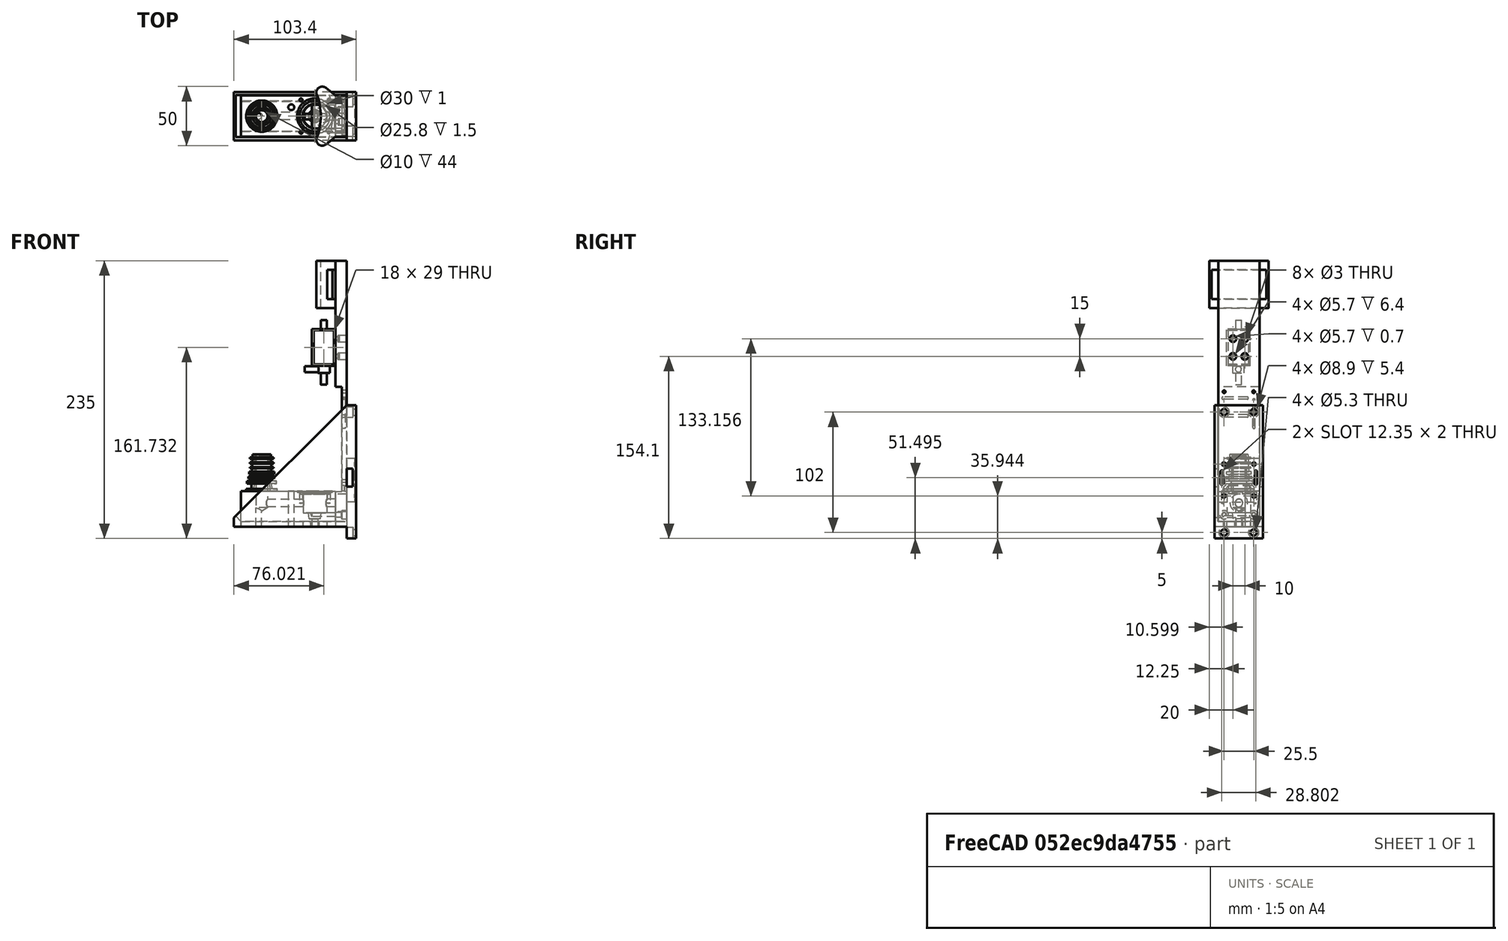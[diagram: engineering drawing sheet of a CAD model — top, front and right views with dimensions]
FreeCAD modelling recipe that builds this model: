
FCSTD DOCUMENT  (FreeCAD 1.0R39109 (Git))
Label: Bottle Nozzle V6
License: All rights reserved
LicenseURL: http://en.wikipedia.org/wiki/All_rights_reserved
objects: Sketcher::SketchObject×31, PartDesign::Pocket×11, PartDesign::Hole×9, PartDesign::Pad×6, Mesh::Feature×5, PartDesign::Body×4, TechDraw::DrawProjGroupItem×3, TechDraw::DrawViewDimension×3, PartDesign::Revolution×2, Spreadsheet::Sheet×1, PartDesign::Groove×1, TechDraw::DrawSVGTemplate×1, TechDraw::DrawPage×1, Part::FeaturePython×1
note: 154 computed .brp shape members not serialized (recipe doc carries the construction recipe); baked Part::Feature solids carry a one-line shape summary decoded from their .brp

FEATURE [Sketcher::SketchObject] Sketch
  ArcFitTolerance = 0
  FullyConstrained = true
  MakeInternals = false
  MapMode = 5
  Placement = pos=(0,0,0) rot=(1,0,0;1.5708rad)
  expr: Constraints[10] = Spreadsheet.HeightPart
  expr: Constraints[12] = Spreadsheet.PartWidth / 2
  expr: Constraints[13] = Spreadsheet.PipeCircle / 2
  expr: Constraints[17] = Spreadsheet.HeigthDop
  expr: Constraints[8] = Spreadsheet.PartWidth2 / 2
  sketch-geometry (8):
    g0: LineSegment StartX=6 StartY=60 StartZ=0 EndX=6.75 EndY=30 EndZ=0
    g1: LineSegment [constr] StartX=6.75 StartY=30 StartZ=0 EndX=17.5 EndY=30 EndZ=0
    g2: LineSegment [constr] StartX=17.5 StartY=30 StartZ=0 EndX=17.5 EndY=0 EndZ=0
    g3: LineSegment [constr] StartX=17.5 StartY=0 StartZ=0 EndX=0 EndY=0 EndZ=0
    g4: LineSegment StartX=0 StartY=60 StartZ=0 EndX=6 EndY=60 EndZ=0
    g5: LineSegment [constr] StartX=0 StartY=60 StartZ=0 EndX=0 EndY=0 EndZ=0
    g6: LineSegment StartX=6.75 StartY=30 StartZ=0 EndX=0 EndY=30 EndZ=0
    g7: LineSegment StartX=0 StartY=30 StartZ=0 EndX=0 EndY=60 EndZ=0
  constraints (23):
    c: Coincident(g0,g1)
    c: Coincident(g1,g2)
    c: Vertical(g2)
    c: Coincident(g2,g3)
    c: Horizontal(g3)
    c: Coincident(g4,g0)
    c: Horizontal(g4)
    c: Horizontal(g1)
    c: DistanceX(g-1,g0) = 6.75
    c: Coincident(g5,g4)
    c: DistanceY(g2,g2) = 30
    c: Vertical(g5)
    c: DistanceX(g-1,g0) = 6
    c: DistanceX(g-1,g2) = 17.5
    c: Coincident(g3,g5)
    c: PointOnObject(g-1,g3)
    c: PointOnObject(g-1,g5)
    c: DistanceY(g1,g0) = 30
    c: Coincident(g6,g0)
    c: PointOnObject(g6,g5)
    c: Horizontal(g6)
    c: Coincident(g7,g6)
    c: Coincident(g7,g4)
FEATURE [PartDesign::Revolution] Revolution
  Angle = 360
  Angle2 = 60
  Axis = (0,2e-16,1)
  Base = (0,0,0)
  Placement = pos=(0,0,0) rot=(1,0,0;1.5708rad)
  Profile = -> Sketch
  ReferenceAxis = -> Sketch [V_Axis]
  Reversed = true
  Suppressed = false
  Type = 0
FEATURE [Spreadsheet::Sheet] Spreadsheet
  cells = A1='DiameterTube; B1(DiameterTube)==5 mm; C1==(B1 / 2) ^ 2 * pi; E1='Outer available; F1==C4 - C1; G1='Similair to inner tube; H1==sqrt(F1 / pi); A2='TubeOffset; B2(TubeOffset)==2.5 mm; C2==(HeightPart - DiameterTube) / 2; A3='DiameterTubeInner; B3(DiameterTubeInner)==B1 - 2 mm; C3==(B3 / 2) ^ 2 * pi; E3='Inner available; F3==C3; H3==sqrt(F3 / pi); A4='DiameterHole; B4(DiameterHole)==10 mm; C4==(B4 / 2) ^ 2 * pi; D4='Max = PartWidth-Walls*2; E4='Ratio liquid VS air surface; F4==F1 / F3; A5='PipeCircle; B5(PipeCircle)==35 mm; A6='HeightPart; B6(HeightPart)==30 mm; A7='HeigthDop; B7(HeigthDop)==30 mm; A8='PartWidth; B8(PartWidth)==12 mm; A9='PartWidth2; B9(PartWidth2)==13.5 mm; A10='MountingHoleDistance; B10(MountingHoleDistance)==round(sqrt((((PipeCircle - PartWidth2) / 2 + PartWidth2) / 2) ^ 2 * 2) / 2.5) * 2.5; A11='OffsetFluidHole2; B11(OffsetFluidHole2)==OffsetFlakte - (4 mm + 0.8 mm * 8 / 2); C11='Blindstop Depth is 3mm+1mm spacer, M5 = 4.2mm; A12='WidthFlank; B12(WidthFlank)==10 mm; A13='OffsetFlakte; B13(OffsetFlakte)==sqrt(PipeCircle ^ 2 - (WidthFlank / 2) ^ 2) / 2 - 0.82 mm; A14='FluidHole; B14(FluidHole)==5 mm; C14='M7; A15='FluidHoleOutsideTube; B15(FluidHoleOutsideTube)==FluidHole + 2 mm; A16='PartOffset; B16(PartOffset)=10; A17='offsetvalve; B17(offsetvalve)=45
FEATURE [Sketcher::SketchObject] Sketch003
  ArcFitTolerance = 0
  AttachmentOffset = pos=(0,0,60) rot=(0,0,1;0rad)
  FullyConstrained = true
  MakeInternals = false
  MapMode = 5
  Placement = pos=(0,0,60) rot=(0,0,1;0rad)
  expr: .AttachmentOffset.Base.z = Spreadsheet.HeightPart + Spreadsheet.HeigthDop
  expr: Constraints[1] = Spreadsheet.DiameterHole
  sketch-geometry (1):
    g0: Circle CenterX=0 CenterY=0 CenterZ=0 NormalX=0 NormalY=0 NormalZ=1 AngleXU=0 Radius=5
  constraints (2):
    c: Coincident(g0,g-1)
    c: Diameter(g0) = 10
FEATURE [Sketcher::SketchObject] Sketch005
  ArcFitTolerance = 0
  FullyConstrained = true
  MakeInternals = false
  MapMode = 5
  expr: Constraints[0] = Spreadsheet.DiameterTube
  expr: Constraints[2] = Spreadsheet.TubeOffset
  sketch-geometry (1):
    g0: Circle CenterX=-2.5 CenterY=0 CenterZ=0 NormalX=0 NormalY=0 NormalZ=1 AngleXU=0 Radius=2.5
  constraints (3):
    c: Diameter(g0) = 5
    c: PointOnObject(g0,g-1)
    c: DistanceX(g0,g-1) = 2.5
FEATURE [Sketcher::SketchObject] Sketch006
  ArcFitTolerance = 0
  FullyConstrained = true
  MakeInternals = false
  MapMode = 5
  expr: Constraints[18] = Spreadsheet.PipeCircle / 2
  expr: Constraints[9] = Spreadsheet.PipeCircle
  sketch-geometry (7):
    g0: LineSegment StartX=0 StartY=17.5 StartZ=0 EndX=62.5 EndY=17.5 EndZ=0
    g1: LineSegment StartX=62.5 StartY=17.5 StartZ=0 EndX=62.5 EndY=-17.5 EndZ=0
    g2: LineSegment StartX=62.5 StartY=-17.5 StartZ=0 EndX=0 EndY=-17.5 EndZ=0
    g3: LineSegment [constr] StartX=0 StartY=-17.5 StartZ=0 EndX=0 EndY=17.5 EndZ=0
    g4: LineSegment StartX=0 StartY=17.5 StartZ=0 EndX=-17.5 EndY=17.5 EndZ=0
    g5: LineSegment StartX=-17.5 StartY=17.5 StartZ=0 EndX=-17.5 EndY=-17.5 EndZ=0
    g6: LineSegment StartX=-17.5 StartY=-17.5 StartZ=0 EndX=0 EndY=-17.5 EndZ=0
  constraints (19):
    c: Coincident(g0,g1)
    c: Coincident(g1,g2)
    c: Coincident(g2,g3)
    c: Coincident(g3,g0)
    c: Horizontal(g0)
    c: Horizontal(g2)
    c: Vertical(g1)
    c: PointOnObject(g0,g-2)
    c: Symmetric(g0,g2,g-1)
    c: DistanceY(g3,g3) = 35
    c: DistanceX(g0,g0) = 62.5  'ww'
    c: Coincident(g0,g4)
    c: Horizontal(g4)
    c: Coincident(g4,g5)
    c: Vertical(g5)
    c: Coincident(g5,g6)
    c: Coincident(g6,g2)
    c: Horizontal(g6)
    c: DistanceX(g4,g4) = 17.5
FEATURE [PartDesign::Pad] Pad
  BaseFeature = -> Revolution
  Direction = (0,0,1)
  Length = 30
  Length2 = 10
  Placement = pos=(0,0,0) rot=(1,0,0;1.5708rad)
  Profile = -> Sketch006
  ReferenceAxis = -> Sketch006 [N_Axis]
  Suppressed = false
  Type = 0
  expr: Length = Spreadsheet.HeightPart
FEATURE [PartDesign::Hole] Hole  label="Hole Combination"
  BaseFeature = -> Pad
  CustomThreadClearance = 0
  Depth = 44
  DepthType = 0
  Diameter = 10
  DrillForDepth = false
  DrillPoint = 1
  DrillPointAngle = 118
  HoleCutCountersinkAngle = 90
  HoleCutCustomValues = false
  HoleCutDepth = 0
  HoleCutDiameter = 10.1
  HoleCutType = 0
  ModelThread = false
  Placement = pos=(0,0,0) rot=(1,0,0;1.5708rad)
  Profile = -> Sketch003
  Suppressed = false
  Tapered = false
  TaperedAngle = 90
  ThreadClass = 0
  ThreadDepth = 44
  ThreadDepthType = 0
  ThreadDirection = 0
  ThreadFit = 0
  ThreadSize = 0
  ThreadType = 0
  Threaded = false
  UseCustomThreadClearance = false
  expr: Depth = 44 mm
FEATURE [PartDesign::Hole] Hole001  label="Hole Air"
  BaseFeature = -> Hole
  CustomThreadClearance = 0
  Depth = 210.228
  DepthType = 1
  Diameter = 5
  DrillForDepth = false
  DrillPoint = 1
  DrillPointAngle = 118
  HoleCutCountersinkAngle = 90
  HoleCutCustomValues = false
  HoleCutDepth = 0
  HoleCutDiameter = 6.1
  HoleCutType = 0
  ModelThread = false
  Placement = pos=(0,0,0) rot=(1,0,0;1.5708rad)
  Profile = -> Sketch005
  Reversed = true
  Suppressed = false
  Tapered = false
  TaperedAngle = 90
  ThreadClass = 0
  ThreadDepth = 210.228
  ThreadDepthType = 0
  ThreadDirection = 0
  ThreadFit = 0
  ThreadSize = 0
  ThreadType = 0
  Threaded = false
  UseCustomThreadClearance = false
FEATURE [Sketcher::SketchObject] Sketch011
  ArcFitTolerance = 0
  AttachmentOffset = pos=(0,0,62.5) rot=(0,0,1;0rad)
  FullyConstrained = true
  MakeInternals = false
  MapMode = 5
  Placement = pos=(62.5,0,0) rot=(0.57735,0.57735,0.57735;2.0944rad)
  expr: .AttachmentOffset.Base.z = Sketch006.Constraints.ww
  expr: .Constraints.hh = 20
  sketch-geometry (1):
    g0: Circle CenterX=0 CenterY=20 CenterZ=0 NormalX=0 NormalY=0 NormalZ=1 AngleXU=0 Radius=4
  constraints (3):
    c: PointOnObject(g0,g-2)
    c: Diameter(g0) = 8
    c: DistanceY(g-1,g0) = 20  'hh'
FEATURE [PartDesign::Hole] Hole002  label="Hole Side"
  BaseFeature = -> Hole001
  CustomThreadClearance = 0
  Depth = 60
  DepthType = 0
  Diameter = 6.4
  DrillForDepth = false
  DrillPoint = 1
  DrillPointAngle = 118
  HoleCutCountersinkAngle = 90
  HoleCutCustomValues = false
  HoleCutDepth = 0
  HoleCutDiameter = 0
  HoleCutType = 0
  ModelThread = false
  Placement = pos=(0,0,0) rot=(1,0,0;1.5708rad)
  Profile = -> Sketch011
  Suppressed = false
  Tapered = false
  TaperedAngle = 90
  ThreadClass = 0
  ThreadDepth = 60
  ThreadDepthType = 0
  ThreadDirection = 0
  ThreadFit = 0
  ThreadSize = 0
  ThreadType = 0
  Threaded = false
  UseCustomThreadClearance = false
  expr: Diameter = 8 * 0.8
FEATURE [Sketcher::SketchObject] Sketch012
  ArcFitTolerance = 0
  AttachmentOffset = pos=(0,0,45) rot=(0,0,1;0rad)
  FullyConstrained = true
  MakeInternals = false
  MapMode = 5
  Placement = pos=(45,0,0) rot=(0.57735,0.57735,0.57735;2.0944rad)
  expr: .AttachmentOffset.Base.z = Spreadsheet.offsetvalve
  expr: Constraints[13] = 25.8 / 2
  expr: Constraints[17] = 20 / 2
  expr: Constraints[24] = 10.8 / 2
  expr: Constraints[25] = 8.6 / 2
  sketch-geometry (15):
    g0: LineSegment StartX=15 StartY=30 StartZ=0 EndX=15 EndY=29 EndZ=0
    g1: LineSegment StartX=15 StartY=29 StartZ=0 EndX=12.9 EndY=29 EndZ=0
    g2: LineSegment StartX=12.9 StartY=29 StartZ=0 EndX=12.9 EndY=27.5 EndZ=0
    g3: LineSegment StartX=12.9 StartY=27.5 StartZ=0 EndX=10.4 EndY=27.5 EndZ=0
    g4: LineSegment StartX=10.4 StartY=27.5 StartZ=0 EndX=10.4 EndY=27.9 EndZ=0
    g5: LineSegment StartX=10 StartY=27.9 StartZ=0 EndX=10 EndY=11.5 EndZ=0
    g6: LineSegment StartX=10 StartY=27.9 StartZ=0 EndX=10.4 EndY=27.9 EndZ=0
    g7: LineSegment StartX=10 StartY=11.5 StartZ=0 EndX=5.4 EndY=11.5 EndZ=0
    g8: LineSegment [constr] StartX=5.4 StartY=11.5 StartZ=0 EndX=4.3 EndY=2.5 EndZ=0
    g9: LineSegment StartX=0 StartY=30 StartZ=0 EndX=0 EndY=0 EndZ=0
    g10: LineSegment StartX=15 StartY=30 StartZ=0 EndX=0 EndY=30 EndZ=0
    g11: LineSegment StartX=2.5 StartY=6.5 StartZ=0 EndX=2.5 EndY=0 EndZ=0
    g12: LineSegment StartX=0 StartY=0 StartZ=0 EndX=2.5 EndY=0 EndZ=0
    g13: LineSegment StartX=5.4 StartY=11.5 StartZ=0 EndX=4.78889 EndY=6.5 EndZ=0
    g14: LineSegment StartX=4.78889 StartY=6.5 StartZ=0 EndX=2.5 EndY=6.5 EndZ=0
  constraints (45):
    c: Vertical(g0)
    c: DistanceY(g-1,g0) = 30
    c: Coincident(g0,g1)
    c: Horizontal(g1)
    c: Coincident(g1,g2)
    c: Vertical(g2)
    c: Coincident(g2,g3)
    c: Coincident(g3,g4)
    c: Vertical(g4)
    c: Vertical(g5)
    c: Horizontal(g3)
    c: DistanceY(g0,g0) = 1
    c: DistanceY(g2,g2) = 1.5
    c: DistanceX(g-1,g1) = 12.9
    c: Coincident(g6,g5)
    c: Coincident(g6,g4)
    c: Horizontal(g6)
    c: DistanceX(g-1,g5) = 10
    c: DistanceY(g4,g4) = 0.4
    c: Equal(g4,g6)
    c: Coincident(g5,g7)
    c: Coincident(g7,g8)
    c: PointOnObject(g9,g-2)
    c: Horizontal(g7)
    c: DistanceX(g-1,g7) = 5.4
    c: DistanceX(g-1,g8) = 4.3
    c: DistanceY(g8,g8) = 9
    c: DistanceY(g5,g3) = 16
    c: DistanceX(g-1,g0) = 15
    c: Coincident(g10,g0)
    c: Coincident(g10,g9)
    c: Horizontal(g10)
    c: DistanceX(g9,g11) = 2.5
    c: PointOnObject(g9,g-2)
    c: PointOnObject(g9,g-1)
    c: PointOnObject(g11,g-1)
    c: Vertical(g11)
    c: Coincident(g12,g9)
    c: Coincident(g12,g11)
    c: Coincident(g13,g7)
    c: PointOnObject(g13,g8)
    c: Coincident(g14,g13)
    c: Horizontal(g14)
    c: DistanceY(g13,g13) = 5
    c: Coincident(g11,g14)
FEATURE [PartDesign::Groove] Groove  label="Groove valve"
  Angle = 360
  Angle2 = 60
  Axis = (1e-16,-1e-16,1)
  Base = (45,0,0)
  BaseFeature = -> Hole002
  Placement = pos=(0,0,0) rot=(1,0,0;1.5708rad)
  Profile = -> Sketch012
  ReferenceAxis = -> Sketch012 [V_Axis]
  Suppressed = false
  Type = 0
FEATURE [Sketcher::SketchObject] Sketch013
  ArcFitTolerance = 0
  AttachmentOffset = pos=(0,0,30) rot=(0,0,1;0rad)
  FullyConstrained = true
  MakeInternals = false
  MapMode = 5
  Placement = pos=(0,0,30) rot=(0,0,1;0rad)
  expr: .AttachmentOffset.Base.z = Spreadsheet.HeightPart
  expr: Constraints[10] = Spreadsheet.offsetvalve
  sketch-geometry (9):
    g0: LineSegment [constr] StartX=33.25 StartY=-13.75 StartZ=0 EndX=33.25 EndY=13.75 EndZ=0
    g1: LineSegment [constr] StartX=33.25 StartY=13.75 StartZ=0 EndX=56.75 EndY=13.75 EndZ=0
    g2: LineSegment [constr] StartX=56.75 StartY=13.75 StartZ=0 EndX=56.75 EndY=-13.75 EndZ=0
    g3: LineSegment [constr] StartX=56.75 StartY=-13.75 StartZ=0 EndX=33.25 EndY=-13.75 EndZ=0
    g4: GeomPoint X=45 Y=-6e-16 Z=0
    g5: Circle CenterX=33.25 CenterY=13.75 CenterZ=0 NormalX=0 NormalY=0 NormalZ=1 AngleXU=0 Radius=1.75
    g6: Circle CenterX=56.75 CenterY=13.75 CenterZ=0 NormalX=0 NormalY=0 NormalZ=1 AngleXU=0 Radius=1.75
    g7: Circle CenterX=33.25 CenterY=-13.75 CenterZ=0 NormalX=0 NormalY=0 NormalZ=1 AngleXU=0 Radius=1.75
    g8: Circle CenterX=56.75 CenterY=-13.75 CenterZ=0 NormalX=0 NormalY=0 NormalZ=1 AngleXU=0 Radius=1.75
  constraints (21):
    c: Coincident(g0,g1)
    c: Coincident(g1,g2)
    c: Coincident(g2,g3)
    c: Coincident(g3,g0)
    c: Horizontal(g1)
    c: Horizontal(g3)
    c: Vertical(g0)
    c: Vertical(g2)
    c: Symmetric(g1,g0,g4)
    c: PointOnObject(g4,g-1)
    c: DistanceX(g-1,g4) = 45
    c: Coincident(g5,g0)
    c: DistanceX(g1,g1) = 23.5
    c: DistanceY(g2,g2) = 27.5
    c: Coincident(g6,g1)
    c: Coincident(g7,g0)
    c: Coincident(g8,g2)
    c: Equal(g5,g6)
    c: Equal(g6,g7)
    c: Equal(g7,g8)
    c: Diameter(g6) = 3.5
FEATURE [PartDesign::Hole] Hole003  label="Hole mouting valve thread"
  BaseFeature = -> Groove
  CustomThreadClearance = 0
  Depth = 10
  DepthType = 0
  Diameter = 2.5
  DrillForDepth = false
  DrillPoint = 1
  DrillPointAngle = 118
  HoleCutCountersinkAngle = 90
  HoleCutCustomValues = false
  HoleCutDepth = 0
  HoleCutDiameter = 6.1
  HoleCutType = 0
  ModelThread = false
  Placement = pos=(0,0,0) rot=(1,0,0;1.5708rad)
  Profile = -> Sketch013
  Suppressed = false
  Tapered = false
  TaperedAngle = 90
  ThreadClass = 0
  ThreadDepth = 10
  ThreadDepthType = 0
  ThreadDirection = 0
  ThreadFit = 0
  ThreadSize = 9
  ThreadType = 1
  Threaded = true
  UseCustomThreadClearance = false
FEATURE [Sketcher::SketchObject] Sketch014
  ArcFitTolerance = 0
  AttachmentOffset = pos=(0,0,62.5) rot=(0,0,1;0rad)
  FullyConstrained = false
  MakeInternals = false
  MapMode = 5
  Placement = pos=(62.5,0,0) rot=(0.57735,0.57735,0.57735;2.0944rad)
  expr: .AttachmentOffset.Base.z = Sketch006.Constraints.ww
  expr: Constraints[1] = Sketch011.Constraints.hh
  sketch-geometry (1):
    g0: Circle CenterX=0 CenterY=20 CenterZ=0 NormalX=0 NormalY=0 NormalZ=1 AngleXU=0 Radius=3.71689
  constraints (2):
    c: PointOnObject(g0,g-2)
    c: DistanceY(g-1,g0) = 20
FEATURE [PartDesign::Hole] Hole004  label="Hole Side thread"
  BaseFeature = -> Hole003
  CustomThreadClearance = 0
  Depth = 20
  DepthType = 0
  Diameter = 6.8
  DrillForDepth = false
  DrillPoint = 1
  DrillPointAngle = 118
  HoleCutCountersinkAngle = 90
  HoleCutCustomValues = false
  HoleCutDepth = 0
  HoleCutDiameter = 6.1
  HoleCutType = 0
  ModelThread = false
  Placement = pos=(0,0,0) rot=(1,0,0;1.5708rad)
  Profile = -> Sketch014
  Suppressed = false
  Tapered = false
  TaperedAngle = 90
  ThreadClass = 0
  ThreadDepth = 20
  ThreadDepthType = 0
  ThreadDirection = 0
  ThreadFit = 0
  ThreadSize = 16
  ThreadType = 1
  Threaded = true
  UseCustomThreadClearance = false
FEATURE [Sketcher::SketchObject] Sketch015
  ArcFitTolerance = 0
  AttachmentOffset = pos=(0,0,4.5) rot=(0,0,1;0rad)
  FullyConstrained = true
  MakeInternals = false
  MapMode = 5
  Placement = pos=(0,0,4.5) rot=(0,0,1;0rad)
  expr: Constraints[14] = Spreadsheet.PipeCircle
  expr: Constraints[15] = Sketch006.Constraints.ww
  expr: Constraints[2] = Spreadsheet.offsetvalve
  sketch-geometry (14):
    g0: Circle CenterX=45 CenterY=0 CenterZ=0 NormalX=0 NormalY=0 NormalZ=1 AngleXU=0 Radius=10
    g1: Circle CenterX=45 CenterY=0 CenterZ=0 NormalX=0 NormalY=0 NormalZ=1 AngleXU=0 Radius=3.5
    g2: LineSegment [constr] StartX=0 StartY=17.5 StartZ=0 EndX=62.5 EndY=17.5 EndZ=0
    g3: LineSegment [constr] StartX=62.5 StartY=17.5 StartZ=0 EndX=62.5 EndY=-17.5 EndZ=0
    g4: LineSegment [constr] StartX=62.5 StartY=-17.5 StartZ=0 EndX=0 EndY=-17.5 EndZ=0
    g5: LineSegment [constr] StartX=0 StartY=-17.5 StartZ=0 EndX=0 EndY=17.5 EndZ=0
    g6: LineSegment StartX=62.5 StartY=17.5 StartZ=0 EndX=-50 EndY=17.5 EndZ=0
    g7: LineSegment StartX=-50 StartY=17.5 StartZ=0 EndX=-50 EndY=12.5 EndZ=0
    g8: LineSegment StartX=-50 StartY=12.5 StartZ=0 EndX=62.5 EndY=12.5 EndZ=0
    g9: LineSegment StartX=62.5 StartY=12.5 StartZ=0 EndX=62.5 EndY=17.5 EndZ=0
    g10: LineSegment StartX=62.5 StartY=-17.5 StartZ=0 EndX=-50 EndY=-17.5 EndZ=0
    g11: LineSegment StartX=-50 StartY=-17.5 StartZ=0 EndX=-50 EndY=-12.5 EndZ=0
    g12: LineSegment StartX=-50 StartY=-12.5 StartZ=0 EndX=62.5 EndY=-12.5 EndZ=0
    g13: LineSegment StartX=62.5 StartY=-12.5 StartZ=0 EndX=62.5 EndY=-17.5 EndZ=0
  constraints (38):
    c: PointOnObject(g0,g-1)
    c: Coincident(g1,g0)
    c: DistanceX(g-1,g0) = 45
    c: Diameter(g1) = 7
    c: Diameter(g0) = 20
    c: Coincident(g2,g3)
    c: Coincident(g3,g4)
    c: Coincident(g4,g5)
    c: Coincident(g5,g2)
    c: Horizontal(g2)
    c: Horizontal(g4)
    c: Vertical(g5)
    c: PointOnObject(g2,g-2)
    c: Symmetric(g2,g3,g-1)
    c: DistanceY(g3,g3) = 35
    c: DistanceX(g2,g2) = 62.5
    c: Coincident(g6,g7)
    c: Coincident(g7,g8)
    c: Coincident(g8,g9)
    c: Coincident(g9,g6)
    c: Horizontal(g6)
    c: Horizontal(g8)
    c: Vertical(g7)
    c: Vertical(g9)
    c: Coincident(g6,g2)
    c: Coincident(g10,g11)
    c: Coincident(g11,g12)
    c: Coincident(g12,g13)
    c: Coincident(g13,g10)
    c: Horizontal(g10)
    c: Horizontal(g12)
    c: Vertical(g11)
    c: Vertical(g13)
    c: Coincident(g10,g3)
    c: Vertical(g11,g7)
    c: DistanceY(g12,g8) = 25
    c: Equal(g7,g11)
    c: DistanceX(g6,g2) = 50
FEATURE [PartDesign::Pocket] Pocket001  label="Pocket fluid outlet pipe"
  BaseFeature = -> Hole004
  Direction = (0,0,-1)
  Length = 5
  Length2 = 5
  Placement = pos=(0,0,0) rot=(1,0,0;1.5708rad)
  Profile = -> Sketch015
  ReferenceAxis = -> Sketch015 [N_Axis]
  Suppressed = false
  Type = 0
FEATURE [Sketcher::SketchObject] Sketch016
  ArcFitTolerance = 0
  AttachmentOffset = pos=(0,0,62.5) rot=(0,0,1;0rad)
  FullyConstrained = false
  MakeInternals = false
  MapMode = 5
  Placement = pos=(62.5,0,0) rot=(0.57735,0.57735,0.57735;2.0944rad)
  sketch-geometry (9):
    g0: LineSegment [constr] StartX=-12.5 StartY=10 StartZ=0 EndX=12.5 EndY=10 EndZ=0
    g1: LineSegment [constr] StartX=12.5 StartY=10 StartZ=0 EndX=12.5 EndY=25 EndZ=0
    g2: LineSegment [constr] StartX=12.5 StartY=25 StartZ=0 EndX=-12.5 EndY=25 EndZ=0
    g3: LineSegment [constr] StartX=-12.5 StartY=25 StartZ=0 EndX=-12.5 EndY=10 EndZ=0
    g4: GeomPoint [constr] X=0 Y=17.5 Z=0
    g5: Circle [constr] CenterX=12.5 CenterY=25 CenterZ=0 NormalX=0 NormalY=0 NormalZ=1 AngleXU=0 Radius=2.9952
    g6: Circle [constr] CenterX=-12.5 CenterY=25 CenterZ=0 NormalX=0 NormalY=0 NormalZ=1 AngleXU=0 Radius=2.9952
    g7: Circle CenterX=-12.5 CenterY=10 CenterZ=0 NormalX=0 NormalY=0 NormalZ=1 AngleXU=0 Radius=2.9952
    g8: Circle CenterX=12.5 CenterY=10 CenterZ=0 NormalX=0 NormalY=0 NormalZ=1 AngleXU=0 Radius=2.9952
  constraints (20):
    c: Coincident(g0,g1)
    c: Coincident(g1,g2)
    c: Coincident(g2,g3)
    c: Coincident(g3,g0)
    c: Horizontal(g0)
    c: Horizontal(g2)
    c: Vertical(g1)
    c: Vertical(g3)
    c: Symmetric(g2,g0,g4)
    c: PointOnObject(g4,g-2)
    c: DistanceX(g2,g2) = 25
    c: DistanceY(g1,g1) = 15
    c: Coincident(g5,g1)
    c: Coincident(g6,g2)
    c: Coincident(g7,g0)
    c: Coincident(g8,g0)
    c: Equal(g5,g8)
    c: Equal(g8,g7)
    c: Equal(g7,g6)
    c: DistanceY(g-1,g0) = 10
FEATURE [PartDesign::Hole] Hole005  label="Hole bottle holder mounting"
  BaseFeature = -> Pocket001
  CustomThreadClearance = 0
  Depth = 20
  DepthType = 0
  Diameter = 3.2
  DrillForDepth = false
  DrillPoint = 1
  DrillPointAngle = 118
  HoleCutCountersinkAngle = 90
  HoleCutCustomValues = false
  HoleCutDepth = 0
  HoleCutDiameter = 6.1
  HoleCutType = 0
  ModelThread = false
  Placement = pos=(0,0,0) rot=(1,0,0;1.5708rad)
  Profile = -> Sketch016
  Refine = true
  Suppressed = false
  Tapered = false
  TaperedAngle = 90
  ThreadClass = 0
  ThreadDepth = 20
  ThreadDepthType = 0
  ThreadDirection = 0
  ThreadFit = 0
  ThreadSize = 0
  ThreadType = 0
  Threaded = false
  UseCustomThreadClearance = false
  expr: Diameter = 0.8 * 4
FEATURE [Sketcher::SketchObject] Sketch018
  ArcFitTolerance = 0
  FullyConstrained = true
  MakeInternals = false
  MapMode = 5
  Placement = pos=(0,0,0) rot=(1,0,0;1.5708rad)
  expr: .Constraints.width = 71.9
  sketch-geometry (15):
    g0: LineSegment StartX=71.9 StartY=102.9 StartZ=0 EndX=-23.5 EndY=7.5 EndZ=0
    g1: LineSegment StartX=-23.5 StartY=7.5 StartZ=0 EndX=-23.5 EndY=0 EndZ=0
    g2: LineSegment StartX=-23.5 StartY=0 StartZ=0 EndX=71.9 EndY=0 EndZ=0
    g3: LineSegment [constr] StartX=71.9 StartY=0 StartZ=0 EndX=71.9 EndY=102.9 EndZ=0
    g4: LineSegment StartX=71.9 StartY=0 StartZ=0 EndX=71.9 EndY=-10 EndZ=0
    g5: Circle [constr] CenterX=-20.7041 CenterY=3.75 CenterZ=0 NormalX=0 NormalY=0 NormalZ=1 AngleXU=0 Radius=1.6
    g6: LineSegment [constr] StartX=-23.5 StartY=7.5 StartZ=0 EndX=-20.5 EndY=7.5 EndZ=0
    g7: LineSegment [constr] StartX=-20.5 StartY=7.5 StartZ=0 EndX=-17.5 EndY=4.5 EndZ=0
    g8: LineSegment [constr] StartX=-23.5 StartY=0 StartZ=0 EndX=-20.7041 EndY=3.75 EndZ=0
    g9: LineSegment [constr] StartX=-20.7041 StartY=3.75 StartZ=0 EndX=-23.5 EndY=7.5 EndZ=0
    g10: LineSegment [constr] StartX=-23.5 StartY=3.75 StartZ=0 EndX=-22.3041 EndY=3.75 EndZ=0
    g11: LineSegment [constr] StartX=-18.727 StartY=5.72703 StartZ=0 EndX=-19.5727 EndY=4.88137 EndZ=0
    g12: LineSegment StartX=71.9 StartY=102.9 StartZ=0 EndX=79.9 EndY=102.9 EndZ=0
    g13: LineSegment StartX=79.9 StartY=102.9 StartZ=0 EndX=79.9 EndY=-10 EndZ=0
    g14: LineSegment StartX=71.9 StartY=-10 StartZ=0 EndX=79.9 EndY=-10 EndZ=0
  constraints (45):
    c: Coincident(g0,g1)
    c: Coincident(g1,g2)
    c: PointOnObject(g3,g-1)
    c: Vertical(g3)
    c: Vertical(g4)
    c: DistanceX(g1,g-1) = 23.5
    c: DistanceY(g1,g1) = 7.5
    c: DistanceX(g-1,g3) = 71.9  'width'
    c: PointOnObject(g-1,g2)
    c: Horizontal(g2)
    c: Vertical(g1)
    c: Coincident(g4,g2)
    c: Vertical(g0,g2)
    c: Angle(g2,g0) = 0.785398
    c: DistanceY(g4,g4) = 10  'MountingHeight'
    c: Diameter(g5) = 3.2
    c: Coincident(g6,g0)
    c: Horizontal(g6)
    c: Coincident(g7,g6)
    c: DistanceX(g6,g6) = 3
    c: DistanceX(g7,g7) = 3
    c: DistanceY(g7,g7) = 3
    c: Coincident(g8,g1)
    c: Coincident(g8,g5)
    c: Coincident(g9,g5)
    c: Coincident(g9,g0)
    c: Equal(g9,g8)
    c: PointOnObject(g10,g1)
    c: PointOnObject(g10,g5)
    c: Horizontal(g10)
    c: PointOnObject(g11,g7)
    c: PointOnObject(g11,g5)
    c: Perpendicular(g7,g11)
    c: Equal(g10,g11)
    c: PointOnObject(g5,g10)
    c: PointOnObject(g5,g11)
    c: Horizontal(g12)
    c: Distance(g12,g12) = 8
    c: Coincident(g12,g13)
    c: Vertical(g13)
    c: Coincident(g14,g4)
    c: Coincident(g14,g13)
    c: Horizontal(g14)
    c: Coincident(g0,g12)
    c: Coincident(g3,g0)
FEATURE [PartDesign::Pad] Pad001  label="Pad all"
  Direction = (0,-1,2e-16)
  Length = 41
  Length2 = 10
  Midplane = true
  Placement = pos=(0,0,0) rot=(1,0,0;1.5708rad)
  Profile = -> Sketch018
  ReferenceAxis = -> Sketch018 [N_Axis]
  Suppressed = false
  Type = 0
  expr: Length = 35 + 3 * 2
FEATURE [Sketcher::SketchObject] Sketch019
  ArcFitTolerance = 0
  FullyConstrained = true
  MakeInternals = false
  MapMode = 5
  Placement = pos=(0,0,0) rot=(1,0,0;1.5708rad)
  expr: Constraints[3] = Sketch018.Constraints.width
  sketch-geometry (5):
    g0: LineSegment StartX=-17.5 StartY=4.5 StartZ=0 EndX=71.9 EndY=4.5 EndZ=0
    g1: LineSegment StartX=71.9 StartY=4.5 StartZ=0 EndX=71.9 EndY=104.5 EndZ=0
    g2: LineSegment StartX=-17.5 StartY=4.5 StartZ=0 EndX=-27.5 EndY=14.5 EndZ=0
    g3: LineSegment StartX=-27.5 StartY=14.5 StartZ=0 EndX=-27.5 EndY=104.5 EndZ=0
    g4: LineSegment StartX=-27.5 StartY=104.5 StartZ=0 EndX=71.9 EndY=104.5 EndZ=0
  constraints (15):
    c: Horizontal(g0)
    c: Coincident(g0,g1)
    c: Vertical(g1)
    c: DistanceX(g-1,g1) = 71.9
    c: DistanceY(g-1,g0) = 4.5
    c: Coincident(g3,g2)
    c: Vertical(g3)
    c: DistanceX(g0,g-1) = 17.5
    c: Coincident(g4,g3)
    c: Coincident(g4,g1)
    c: Horizontal(g4)
    c: Angle(g0,g2) = 2.35619
    c: Coincident(g2,g0)
    c: DistanceX(g2,g2) = 10
    c: DistanceY(g1,g1) = 100
FEATURE [PartDesign::Pocket] Pocket  label="Pocket 1"
  BaseFeature = -> Pad001
  Direction = (0,1,-2e-16)
  Length = 35.6
  Length2 = 5
  Midplane = true
  Placement = pos=(0,0,0) rot=(1,0,0;1.5708rad)
  Profile = -> Sketch019
  ReferenceAxis = -> Sketch019 [N_Axis]
  Suppressed = false
  Type = 0
  expr: Length = 35 + 0.6
FEATURE [Sketcher::SketchObject] Sketch020
  ArcFitTolerance = 0
  FullyConstrained = true
  MakeInternals = false
  MapMode = 5
  Placement = pos=(0,0,0) rot=(1,0,0;1.5708rad)
  expr: Constraints[10] = 17.5 mm + 0.25 mm
  expr: Constraints[11] = Sketch018.Constraints.width
  sketch-geometry (4):
    g0: LineSegment StartX=-17.75 StartY=5 StartZ=0 EndX=71.9 EndY=5 EndZ=0
    g1: LineSegment StartX=71.9 StartY=5 StartZ=0 EndX=71.9 EndY=0 EndZ=0
    g2: LineSegment StartX=71.9 StartY=0 StartZ=0 EndX=-17.75 EndY=0 EndZ=0
    g3: LineSegment StartX=-17.75 StartY=0 StartZ=0 EndX=-17.75 EndY=5 EndZ=0
  constraints (12):
    c: Coincident(g0,g1)
    c: Coincident(g1,g2)
    c: Coincident(g2,g3)
    c: Coincident(g3,g0)
    c: Horizontal(g0)
    c: Horizontal(g2)
    c: Vertical(g1)
    c: Vertical(g3)
    c: PointOnObject(g1,g-1)
    c: DistanceY(g3,g3) = 5
    c: DistanceX(g2,g-1) = 17.75
    c: DistanceX(g-1,g1) = 71.9
FEATURE [PartDesign::Pocket] Pocket002  label="Pocket 2"
  BaseFeature = -> Pocket
  Direction = (0,1,-2e-16)
  Length = 25.6
  Length2 = 5
  Midplane = true
  Placement = pos=(0,0,0) rot=(1,0,0;1.5708rad)
  Profile = -> Sketch020
  ReferenceAxis = -> Sketch020 [N_Axis]
  Suppressed = false
  Type = 0
  expr: Length = 25 + 0.6
FEATURE [Sketcher::SketchObject] Sketch021
  ArcFitTolerance = 0
  AttachmentOffset = pos=(0,0,69.5) rot=(0,0,1;0rad)
  FullyConstrained = false
  MakeInternals = false
  MapMode = 5
  Placement = pos=(71.9,0,0) rot=(0.57735,0.57735,0.57735;2.0944rad)
  expr: .Placement.Base.x = Sketch018.Constraints.width
  expr: Constraints[9] = Sketch018.Constraints.MountingHeight / 2
  sketch-geometry (4):
    g0: Circle CenterX=-12.5 CenterY=97 CenterZ=0 NormalX=0 NormalY=0 NormalZ=1 AngleXU=0 Radius=1.77352
    g1: Circle CenterX=12.5 CenterY=97 CenterZ=0 NormalX=0 NormalY=0 NormalZ=1 AngleXU=0 Radius=1.77352
    g2: Circle CenterX=-12.5 CenterY=-5 CenterZ=0 NormalX=0 NormalY=0 NormalZ=1 AngleXU=0 Radius=1.77352
    g3: Circle CenterX=12.5 CenterY=-5 CenterZ=0 NormalX=0 NormalY=0 NormalZ=1 AngleXU=0 Radius=1.77352
  constraints (10):
    c: Symmetric(g0,g1,g-2)
    c: DistanceX(g0,g1) = 25
    c: Equal(g0,g1)
    c: DistanceY(g-1,g1) = 97
    c: Horizontal(g2,g3)
    c: Vertical(g0,g2)
    c: Vertical(g3,g1)
    c: Equal(g0,g2)
    c: Equal(g3,g2)
    c: DistanceY(g2,g-1) = 5
FEATURE [PartDesign::Hole] Hole006  label="Mounting holes"
  BaseFeature = -> Pocket002
  CustomThreadClearance = 0
  Depth = 320.149
  DepthType = 1
  Diameter = 5.3
  DrillForDepth = false
  DrillPoint = 1
  DrillPointAngle = 118
  HoleCutCountersinkAngle = 90
  HoleCutCustomValues = false
  HoleCutDepth = 5.4
  HoleCutDiameter = 8.9
  HoleCutType = 1
  ModelThread = false
  Placement = pos=(0,0,0) rot=(1,0,0;1.5708rad)
  Profile = -> Sketch021
  Reversed = true
  Suppressed = false
  Tapered = false
  TaperedAngle = 90
  ThreadClass = 0
  ThreadDepth = 320.149
  ThreadDepthType = 0
  ThreadDirection = 0
  ThreadFit = 0
  ThreadSize = 0
  ThreadType = 0
  Threaded = false
  UseCustomThreadClearance = false
FEATURE [Sketcher::SketchObject] Sketch022
  ArcFitTolerance = 0
  AttachmentOffset = pos=(0,0,62.5) rot=(0,0,1;0rad)
  FullyConstrained = true
  MakeInternals = false
  MapMode = 5
  Placement = pos=(62.5,0,0) rot=(0.57735,0.57735,0.57735;2.0944rad)
  expr: .Constraints.Width = 35 mm
  expr: .Constraints.magA = 20.2 mm + 0.2 mm * 2
  expr: .Constraints.magA2 = 4.2 mm + 0.2 mm * 2
  expr: Constraints[12] = 4.5 mm + 0.2 mm
  expr: Constraints[23] = 5 + 0.2
  expr: Constraints[57] = 0.75 * 3
  expr: Constraints[59] = 29.5 - 4.5
  expr: Constraints[60] = 84 - 8.25
  sketch-geometry (24):
    g0: LineSegment StartX=-17.5 StartY=225 StartZ=0 EndX=-17.5 EndY=4.7 EndZ=0
    g1: LineSegment StartX=-12.3 StartY=0 StartZ=0 EndX=12.3 EndY=0 EndZ=0
    g2: LineSegment StartX=17.5 StartY=4.7 StartZ=0 EndX=17.5 EndY=225 EndZ=0
    g3: LineSegment StartX=17.5 StartY=225 StartZ=0 EndX=-17.5 EndY=225 EndZ=0
    g4: GeomPoint [constr] X=0 Y=76.325 Z=0
    g5: LineSegment StartX=-12.3 StartY=4.7 StartZ=0 EndX=-12.3 EndY=0 EndZ=0
    g6: LineSegment StartX=12.3 StartY=0 StartZ=0 EndX=12.3 EndY=4.7 EndZ=0
    g7: LineSegment StartX=-17.5 StartY=4.7 StartZ=0 EndX=-12.3 EndY=4.7 EndZ=0
    g8: LineSegment StartX=12.3 StartY=4.7 StartZ=0 EndX=17.5 EndY=4.7 EndZ=0
    g9: ArcOfCircle CenterX=-8 CenterY=32.4 CenterZ=0 NormalX=0 NormalY=0 NormalZ=1 AngleXU=0 Radius=2.3 StartAngle=1.5708 EndAngle=4.71239
    g10: ArcOfCircle CenterX=8 CenterY=32.4 CenterZ=0 NormalX=0 NormalY=0 NormalZ=1 AngleXU=0 Radius=2.3 StartAngle=4.71239 EndAngle=7.85398
    g11: LineSegment StartX=-8 StartY=34.7 StartZ=0 EndX=8 EndY=34.7 EndZ=0
    g12: LineSegment StartX=-8 StartY=30.1 StartZ=0 EndX=8 EndY=30.1 EndZ=0
    g13: LineSegment [constr] StartX=-10.3 StartY=32.4 StartZ=0 EndX=10.3 EndY=32.4 EndZ=0
    g14: Circle CenterX=0 CenterY=20 CenterZ=0 NormalX=0 NormalY=0 NormalZ=1 AngleXU=0 Radius=7.5
    g15: LineSegment [constr] StartX=-12.5 StartY=38.45 StartZ=0 EndX=12.5 EndY=38.45 EndZ=0
    g16: LineSegment [constr] StartX=12.5 StartY=38.45 StartZ=0 EndX=12.5 EndY=114.2 EndZ=0
    g17: LineSegment [constr] StartX=12.5 StartY=114.2 StartZ=0 EndX=-12.5 EndY=114.2 EndZ=0
    g18: LineSegment [constr] StartX=-12.5 StartY=114.2 StartZ=0 EndX=-12.5 EndY=38.45 EndZ=0
    g19: GeomPoint [constr] X=0 Y=76.325 Z=0
    g20: Circle CenterX=-12.5 CenterY=114.2 CenterZ=0 NormalX=0 NormalY=0 NormalZ=1 AngleXU=0 Radius=1.125
    g21: Circle CenterX=12.5 CenterY=114.2 CenterZ=0 NormalX=0 NormalY=0 NormalZ=1 AngleXU=0 Radius=1.125
    g22: Circle CenterX=-12.5 CenterY=38.45 CenterZ=0 NormalX=0 NormalY=0 NormalZ=1 AngleXU=0 Radius=1.125
    g23: Circle CenterX=12.5 CenterY=38.45 CenterZ=0 NormalX=0 NormalY=0 NormalZ=1 AngleXU=0 Radius=1.125
  constraints (61):
    c: Coincident(g2,g3)
    c: Coincident(g3,g0)
    c: Vertical(g0)
    c: Vertical(g2)
    c: Horizontal(g1)
    c: Horizontal(g3)
    c: PointOnObject(g4,g-2)
    c: Vertical(g5)
    c: Vertical(g6)
    c: Coincident(g1,g5)
    c: Coincident(g1,g6)
    c: DistanceX(g0,g2) = 35  'Width'
    c: DistanceY(g6,g6) = 4.7
    c: PointOnObject(g-1,g1)
    c: Symmetric(g2,g0,g-2)
    c: DistanceY(g-1,g2) = 225  'height'
    c: Coincident(g7,g0)
    c: Horizontal(g7)
    c: Coincident(g8,g6)
    c: Coincident(g8,g2)
    c: Horizontal(g8)
    c: Equal(g7,g8)
    c: Coincident(g5,g7)
    c: DistanceX(g8,g8) = 5.2
    c: Tangent(g9,g11) = 1.5708
    c: Tangent(g9,g12) = -1.5708
    c: Tangent(g10,g11) = 1.5708
    c: Tangent(g10,g12) = -1.5708
    c: Equal(g9,g10)
    c: Symmetric(g10,g9,g-2)
    c: DistanceY(g9,g9) = 4.6  'magA2'
    c: Horizontal(g13)
    c: PointOnObject(g13,g9)
    c: PointOnObject(g13,g10)
    c: PointOnObject(g9,g13)
    c: DistanceX(g13,g13) = 20.6  'magA'
    c: DistanceY(g-1,g9) = 32.4  'magnetoffset'
    c: PointOnObject(g14,g-2)
    c: DistanceY(g-1,g14) = 20
    c: Diameter(g14) = 15
    c: Coincident(g15,g16)
    c: Coincident(g16,g17)
    c: Coincident(g17,g18)
    c: Coincident(g18,g15)
    c: Horizontal(g15)
    c: Horizontal(g17)
    c: Vertical(g16)
    c: Vertical(g18)
    c: Symmetric(g17,g15,g19)
    c: Coincident(g19,g4)
    c: Coincident(g20,g17)
    c: Coincident(g21,g16)
    c: Coincident(g22,g15)
    c: Coincident(g23,g15)
    c: Equal(g22,g23)
    c: Equal(g23,g21)
    c: Equal(g21,g20)
    c: Diameter(g20) = 2.25
    c: DistanceY(g-1,g17) = 114.2
    c: DistanceX(g17,g17) = 25
    c: DistanceY(g18,g18) = 75.75
FEATURE [PartDesign::Pad] Pad002  label="Pad All"
  Direction = (1,1e-16,-1e-16)
  Length = 9.4
  Length2 = 10
  Placement = pos=(62.5,0,0) rot=(0.57735,0.57735,0.57735;2.0944rad)
  Profile = -> Sketch022
  ReferenceAxis = -> Sketch022 [N_Axis]
  Refine = true
  Suppressed = false
  Type = 0
FEATURE [Sketcher::SketchObject] Sketch023
  ArcFitTolerance = 0
  AttachmentOffset = pos=(0,0,69.5) rot=(0,0,1;0rad)
  FullyConstrained = true
  MakeInternals = false
  MapMode = 5
  Placement = pos=(71.9,0,0) rot=(0.57735,0.57735,0.57735;2.0944rad)
  expr: .AttachmentOffset.Base.z = 62.5 mm + 7 mm
  expr: .Placement.Base.x = Sketch018.Constraints.width
  sketch-geometry (9):
    g0: LineSegment [constr] StartX=-12.5 StartY=10 StartZ=0 EndX=12.5 EndY=10 EndZ=0
    g1: LineSegment [constr] StartX=12.5 StartY=10 StartZ=0 EndX=12.5 EndY=25 EndZ=0
    g2: LineSegment [constr] StartX=12.5 StartY=25 StartZ=0 EndX=-12.5 EndY=25 EndZ=0
    g3: LineSegment [constr] StartX=-12.5 StartY=25 StartZ=0 EndX=-12.5 EndY=10 EndZ=0
    g4: GeomPoint [constr] X=0 Y=17.5 Z=0
    g5: Circle [constr] CenterX=-12.5 CenterY=25 CenterZ=0 NormalX=0 NormalY=0 NormalZ=1 AngleXU=0 Radius=2.5
    g6: Circle CenterX=-12.5 CenterY=10 CenterZ=0 NormalX=0 NormalY=0 NormalZ=1 AngleXU=0 Radius=2.5
    g7: Circle CenterX=12.5 CenterY=10 CenterZ=0 NormalX=0 NormalY=0 NormalZ=1 AngleXU=0 Radius=2.5
    g8: Circle [constr] CenterX=12.5 CenterY=25 CenterZ=0 NormalX=0 NormalY=0 NormalZ=1 AngleXU=0 Radius=2.5
  constraints (21):
    c: Coincident(g0,g1)
    c: Coincident(g1,g2)
    c: Coincident(g2,g3)
    c: Coincident(g3,g0)
    c: Horizontal(g0)
    c: Horizontal(g2)
    c: Vertical(g1)
    c: Vertical(g3)
    c: Symmetric(g2,g0,g4)
    c: PointOnObject(g4,g-2)
    c: DistanceX(g2,g2) = 25
    c: DistanceY(g1,g1) = 15
    c: DistanceY(g-1,g0) = 10
    c: Coincident(g5,g2)
    c: Coincident(g6,g0)
    c: Coincident(g7,g0)
    c: Coincident(g8,g1)
    c: Equal(g5,g6)
    c: Equal(g6,g7)
    c: Equal(g7,g8)
    c: Diameter(g8) = 5
FEATURE [PartDesign::Hole] Hole007  label="Hole mounting to nozzle"
  BaseFeature = -> Pad002
  CustomThreadClearance = 0
  Depth = 460.358
  DepthType = 1
  Diameter = 4
  DrillForDepth = false
  DrillPoint = 1
  DrillPointAngle = 118
  HoleCutCountersinkAngle = 90
  HoleCutCustomValues = false
  HoleCutDepth = 4.2
  HoleCutDiameter = 7.2
  HoleCutType = 1
  ModelThread = false
  Placement = pos=(62.5,0,0) rot=(0.57735,0.57735,0.57735;2.0944rad)
  Profile = -> Sketch023
  Refine = true
  Suppressed = false
  Tapered = false
  TaperedAngle = 90
  ThreadClass = 0
  ThreadDepth = 460.358
  ThreadDepthType = 0
  ThreadDirection = 0
  ThreadFit = 0
  ThreadSize = 0
  ThreadType = 0
  Threaded = false
  UseCustomThreadClearance = false
  expr: Diameter = 4
FEATURE [Mesh::Feature] Magnet_pogo_5pin  label="Magnet pogo 5pin male"
  Placement = pos=(73.8595,0.1,32.3976) rot=(0.57735,-0.57735,-0.57735;2.0944rad)
  expr: .Placement.Base.x = Sketch018.Constraints.width
FEATURE [Mesh::Feature] Magnet_pogo_5pin_female  label="Magnet pogo 5pin female"
  Placement = pos=(69.8269,0.1,32.3924) rot=(0.57735,0.57735,0.57735;2.0944rad)
FEATURE [Sketcher::SketchObject] Sketch027
  ArcFitTolerance = 0
  AttachmentOffset = pos=(0,0,225) rot=(0,0,1;0rad)
  FullyConstrained = true
  MakeInternals = false
  MapMode = 5
  Placement = pos=(0,0,225) rot=(0,0,1;0rad)
  expr: .AttachmentOffset.Base.z = Sketch022.Constraints.height
  expr: Constraints[8] = 62.5 mm
  sketch-geometry (6):
    g0: ArcOfCircle CenterX=0 CenterY=0 CenterZ=0 NormalX=0 NormalY=0 NormalZ=1 AngleXU=0 Radius=50 StartAngle=5.91102 EndAngle=6.65535
    g1: ArcOfCircle CenterX=51.2348 CenterY=20 CenterZ=0 NormalX=0 NormalY=0 NormalZ=1 AngleXU=0 Radius=5 StartAngle=0.904261 EndAngle=3.51376
    g2: ArcOfCircle CenterX=51.2348 CenterY=-20 CenterZ=0 NormalX=0 NormalY=0 NormalZ=1 AngleXU=0 Radius=5 StartAngle=2.76942 EndAngle=5.37892
    g3: LineSegment StartX=62.5 StartY=17.5 StartZ=0 EndX=62.5 EndY=-17.5 EndZ=0
    g4: LineSegment StartX=62.5 StartY=-17.5 StartZ=0 EndX=54.3261 EndY=-23.9298 EndZ=0
    g5: LineSegment StartX=54.3261 StartY=23.9298 StartZ=0 EndX=62.5 EndY=17.5 EndZ=0
  constraints (15):
    c: Coincident(g0,g-1)
    c: Vertical(g1,g2)
    c: Equal(g1,g2)
    c: Radius(g0) = 50
    c: Tangent(g1,g0) = 1.5708
    c: Tangent(g2,g0) = 1.5708
    c: Symmetric(g3,g3,g-1)
    c: DistanceY(g3,g3) = 35
    c: DistanceX(g-1,g3) = 62.5
    c: DistanceY(g2,g1) = 40
    c: Coincident(g4,g3)
    c: Tangent(g4,g2) = 1.5708
    c: Coincident(g5,g3)
    c: Tangent(g5,g1) = 1.5708
    c: Radius(g1) = 5
FEATURE [Sketcher::SketchObject] Sketch028
  ArcFitTolerance = 0
  AttachmentOffset = pos=(0,0,205) rot=(0,0,1;0rad)
  FullyConstrained = true
  MakeInternals = false
  MapMode = 5
  Placement = pos=(0,0,205) rot=(0,0,1;0rad)
  expr: .AttachmentOffset.Base.z = Sketch022.Constraints.height - 20 mm
  sketch-geometry (4):
    g0: ArcOfCircle CenterX=0 CenterY=0 CenterZ=0 NormalX=0 NormalY=0 NormalZ=1 AngleXU=0 Radius=60 StartAngle=5.75959 EndAngle=6.80678
    g1: LineSegment StartX=51.9615 StartY=30 StartZ=0 EndX=62.5 EndY=30 EndZ=0
    g2: LineSegment StartX=62.5 StartY=30 StartZ=0 EndX=62.5 EndY=-30 EndZ=0
    g3: LineSegment StartX=62.5 StartY=-30 StartZ=0 EndX=51.9615 EndY=-30 EndZ=0
  constraints (11):
    c: Coincident(g0,g-1)
    c: Coincident(g1,g2)
    c: Coincident(g2,g3)
    c: Horizontal(g3)
    c: Coincident(g0,g1)
    c: Coincident(g0,g3)
    c: Symmetric(g1,g2,g-1)
    c: Horizontal(g1)
    c: Radius(g0) = 60
    c: DistanceX(g-1,g1) = 62.5
    c: DistanceY(g2,g2) = 60
FEATURE [Sketcher::SketchObject] Sketch029
  ArcFitTolerance = 0
  FullyConstrained = true
  MakeInternals = false
  MapMode = 5
  expr: Constraints[2] = 7.5
  sketch-geometry (1):
    g0: Circle CenterX=25 CenterY=7.5 CenterZ=0 NormalX=0 NormalY=0 NormalZ=1 AngleXU=0 Radius=2.5
  constraints (3):
    c: Diameter(g0) = 5
    c: DistanceX(g-1,g0) = 25
    c: DistanceY(g-1,g0) = 7.5
FEATURE [PartDesign::Pocket] Pocket007  label="Pocket air though hole"
  BaseFeature = -> Hole005
  Direction = (0,0,-1)
  Length = 5
  Length2 = 5
  Placement = pos=(0,0,0) rot=(1,0,0;1.5708rad)
  Profile = -> Sketch029
  ReferenceAxis = -> Sketch029 [N_Axis]
  Refine = true
  Reversed = true
  Suppressed = false
  Type = 1
FEATURE [PartDesign::Body] Body  label="Bottle Nozzle"
  AllowCompound = false
  Group = -> [Sketch,Revolution,Sketch003,Sketch005,Sketch006,Pad,Hole,Hole001,Sketch011,Hole002,Sketch012,Groove,Sketch013,Hole003,Sketch014,Hole004,Sketch015,Pocket001,Sketch016,Hole005,Sketch029,Pocket007]
  Origin = -> Origin
  Tip = -> Pocket007
FEATURE [Mesh::Feature] Coil_46_008_112  label="Coil 46.008.112"
  Placement = pos=(45,0,41.2) rot=(0,0,1;0rad)
FEATURE [Sketcher::SketchObject] Sketch030
  ArcFitTolerance = 0
  AttachmentOffset = pos=(0,0,62.5) rot=(0,0,1;0rad)
  FullyConstrained = true
  MakeInternals = false
  MapMode = 5
  Placement = pos=(62.5,0,0) rot=(0.57735,0.57735,0.57735;2.0944rad)
  expr: Constraints[11] = Sketch022.Constraints.Width
  expr: Constraints[7] = 30 - 0.2
  expr: Constraints[8] = 88 mm + 0.2 mm * 2
  sketch-geometry (4):
    g0: LineSegment StartX=-17.5 StartY=118.2 StartZ=0 EndX=-17.5 EndY=29.8 EndZ=0
    g1: LineSegment StartX=-17.5 StartY=29.8 StartZ=0 EndX=17.5 EndY=29.8 EndZ=0
    g2: LineSegment StartX=17.5 StartY=29.8 StartZ=0 EndX=17.5 EndY=118.2 EndZ=0
    g3: LineSegment StartX=17.5 StartY=118.2 StartZ=0 EndX=-17.5 EndY=118.2 EndZ=0
  constraints (12):
    c: Coincident(g0,g1)
    c: Coincident(g1,g2)
    c: Coincident(g2,g3)
    c: Coincident(g3,g0)
    c: Vertical(g0)
    c: Vertical(g2)
    c: Horizontal(g1)
    c: DistanceY(g-1,g1) = 29.8
    c: DistanceY(g0,g0) = 88.4
    c: DistanceY(g-1,g2) = 118.2  'PCBhieght'
    c: Symmetric(g0,g2,g-2)
    c: DistanceX(g3,g3) = 35
FEATURE [TechDraw::DrawSVGTemplate] Template
  Height = 210
  Orientation = 1
  Width = 297
FEATURE [TechDraw::DrawProjGroupItem] View
  CoarseView = false
  Direction = (0,-1,0)
  Focus = 100
  HardHidden = false
  IsoCount = 0
  IsoHidden = false
  IsoVisible = false
  LockPosition = false
  Perspective = false
  Rotation = 0
  RotationVector = (1,0,0)
  ScaleType = 0
  ScrubCount = 1
  SeamHidden = false
  SeamVisible = false
  SmoothHidden = false
  SmoothVisible = true
  Source = -> [Body]
  Type = 0
  X = 123.469
  XDirection = (1,0,0)
  Y = 88.6339
FEATURE [TechDraw::DrawProjGroupItem] View001
  CoarseView = false
  Direction = (1,3e-16,0)
  Focus = 100
  HardHidden = false
  IsoCount = 0
  IsoHidden = false
  IsoVisible = false
  LockPosition = false
  Perspective = false
  Rotation = 0
  RotationVector = (1,0,0)
  ScaleType = 0
  ScrubCount = 1
  SeamHidden = false
  SeamVisible = false
  SmoothHidden = false
  SmoothVisible = true
  Source = -> [Body]
  Type = 0
  X = 203.696
  XDirection = (-3e-16,1,0)
  Y = 88.6339
FEATURE [TechDraw::DrawProjGroupItem] View002
  CoarseView = false
  Direction = (0,0,1)
  Focus = 100
  HardHidden = false
  IsoCount = 0
  IsoHidden = false
  IsoVisible = false
  LockPosition = false
  Perspective = false
  Rotation = 0
  RotationVector = (1,0,0)
  ScaleType = 0
  ScrubCount = 1
  SeamHidden = false
  SeamVisible = false
  SmoothHidden = false
  SmoothVisible = true
  Source = -> [Body]
  Type = 0
  X = 123.469
  XDirection = (1,0,0)
  Y = 168.86
FEATURE [TechDraw::DrawViewDimension] Dimension
  AngleOverride = false
  Arbitrary = true
  ArbitraryTolerances = false
  EqualTolerance = true
  ExtensionAngle = 0
  FormatSpec = 4x M4
  FormatSpecOverTolerance = %+.2w
  FormatSpecUnderTolerance = %+.2w
  Inverted = false
  LineAngle = 0
  LockPosition = false
  MeasureType = 1
  OverTolerance = 0
  References2D = -> [View002]
  Rotation = 0
  ScaleType = 0
  TheoreticalExact = false
  Type = 5
  UnderTolerance = 0
  X = 56.3566
  Y = 21.4879
FEATURE [TechDraw::DrawViewDimension] Dimension001
  AngleOverride = false
  Arbitrary = true
  ArbitraryTolerances = false
  EqualTolerance = true
  ExtensionAngle = 0
  FormatSpec = 2x M4
  FormatSpecOverTolerance = %+.2w
  FormatSpecUnderTolerance = %+.2w
  Inverted = false
  LineAngle = 0
  LockPosition = false
  MeasureType = 1
  OverTolerance = 0
  References2D = -> [View001]
  Rotation = 0
  ScaleType = 0
  TheoreticalExact = false
  Type = 5
  UnderTolerance = 0
  X = 35.5629
  Y = -8.67711
FEATURE [TechDraw::DrawViewDimension] Dimension002
  AngleOverride = false
  Arbitrary = true
  ArbitraryTolerances = false
  EqualTolerance = true
  ExtensionAngle = 0
  FormatSpec = M8 10mm depth
  FormatSpecOverTolerance = %+.2w
  FormatSpecUnderTolerance = %+.2w
  Inverted = false
  LineAngle = 0
  LockPosition = false
  MeasureType = 1
  OverTolerance = 0
  References2D = -> [View001]
  Rotation = 0
  ScaleType = 0
  TheoreticalExact = false
  Type = 5
  UnderTolerance = 0
  X = 43.3565
  Y = 8.97265
FEATURE [TechDraw::DrawPage] Page  label="Bottle Nozzle threads"
  KeepUpdated = true
  NextBalloonIndex = 1
  ProjectionType = 0
  Template = -> Template
  Views = -> [View,View001,View002,Dimension,Dimension001,Dimension002]
FEATURE [Sketcher::SketchObject] Sketch026
  ArcFitTolerance = 0
  AttachmentOffset = pos=(0,0,62.5) rot=(0,0,1;0rad)
  FullyConstrained = true
  MakeInternals = false
  MapMode = 5
  Placement = pos=(69.9,0,0) rot=(0.57735,0.57735,0.57735;2.0944rad)
  expr: .AttachmentOffset.Base.z = 62.5 mm
  expr: .Constraints.magB = 25.9 + 0.2 * 2
  expr: .Constraints.magB2 = 4.3 mm + 0.2 mm * 2
  expr: Constraints[12] = Sketch022.Constraints.magnetoffset
  sketch-geometry (5):
    g0: ArcOfCircle CenterX=-10.8 CenterY=32.4 CenterZ=0 NormalX=0 NormalY=0 NormalZ=1 AngleXU=0 Radius=2.35 StartAngle=1.5708 EndAngle=4.71239
    g1: ArcOfCircle CenterX=10.8 CenterY=32.4 CenterZ=0 NormalX=0 NormalY=0 NormalZ=1 AngleXU=0 Radius=2.35 StartAngle=4.71239 EndAngle=7.85398
    g2: LineSegment StartX=-10.8 StartY=34.75 StartZ=0 EndX=10.8 EndY=34.75 EndZ=0
    g3: LineSegment StartX=-10.8 StartY=30.05 StartZ=0 EndX=10.8 EndY=30.05 EndZ=0
    g4: LineSegment [constr] StartX=-13.15 StartY=32.4 StartZ=0 EndX=13.15 EndY=32.4 EndZ=0
  constraints (13):
    c: Tangent(g0,g2) = 1.5708
    c: Tangent(g0,g3) = -1.5708
    c: Tangent(g1,g2) = 1.5708
    c: Tangent(g1,g3) = -1.5708
    c: Equal(g0,g1)
    c: Symmetric(g1,g0,g-2)
    c: DistanceY(g0,g0) = 4.7  'magB2'
    c: Horizontal(g4)
    c: PointOnObject(g4,g0)
    c: PointOnObject(g4,g1)
    c: PointOnObject(g1,g4)
    c: DistanceX(g4,g4) = 26.3  'magB'
    c: DistanceY(g-1,g4) = 32.4
FEATURE [PartDesign::Pocket] Pocket005  label="Pocket magnet"
  BaseFeature = -> Hole007
  Direction = (-1,-1e-16,1e-16)
  Length = 5
  Length2 = 5
  Placement = pos=(62.5,0,0) rot=(0.57735,0.57735,0.57735;2.0944rad)
  Profile = -> Sketch026
  ReferenceAxis = -> Sketch026 [N_Axis]
  Refine = true
  Suppressed = false
  Type = 0
FEATURE [PartDesign::Pad] Pad003  label="Pad bottle mount"
  BaseFeature = -> Pocket005
  Direction = (0,0,1)
  Length = 40
  Length2 = 10
  Placement = pos=(62.5,0,0) rot=(0.57735,0.57735,0.57735;2.0944rad)
  Profile = -> Sketch027
  ReferenceAxis = -> Sketch027 [N_Axis]
  Refine = true
  Reversed = true
  Suppressed = false
  Type = 0
  expr: Length = 40
FEATURE [PartDesign::Pocket] Pocket006  label="Pocket velcro hole"
  BaseFeature = -> Pad003
  Direction = (0,0,-1)
  Length = 25
  Length2 = 5
  Midplane = true
  Placement = pos=(62.5,0,0) rot=(0.57735,0.57735,0.57735;2.0944rad)
  Profile = -> Sketch028
  ReferenceAxis = -> Sketch028 [N_Axis]
  Refine = true
  Suppressed = false
  Type = 0
FEATURE [PartDesign::Pocket] Pocket008  label="Pocket PCB"
  BaseFeature = -> Pocket006
  Direction = (-1,-1e-16,1e-16)
  Length = 5.3
  Length2 = 5
  Placement = pos=(62.5,0,0) rot=(0.57735,0.57735,0.57735;2.0944rad)
  Profile = -> Sketch030
  ReferenceAxis = -> Sketch030 [N_Axis]
  Refine = true
  Reversed = true
  Suppressed = false
  Type = 0
FEATURE [Sketcher::SketchObject] Sketch031
  ArcFitTolerance = 0
  AttachmentOffset = pos=(0,0,62.5) rot=(0,0,1;0rad)
  FullyConstrained = false
  MakeInternals = false
  MapMode = 5
  Placement = pos=(62.5,0,0) rot=(0.57735,0.57735,0.57735;2.0944rad)
  sketch-geometry (12):
    g0: ArcOfCircle CenterX=12.7832 CenterY=107.278 CenterZ=0 NormalX=0 NormalY=0 NormalZ=1 AngleXU=0 Radius=1.06277 StartAngle=1e-16 EndAngle=3.14159
    g1: ArcOfCircle CenterX=12.7832 CenterY=84.0303 CenterZ=0 NormalX=0 NormalY=0 NormalZ=1 AngleXU=0 Radius=1.06277 StartAngle=3.14159 EndAngle=6.28319
    g2: LineSegment StartX=13.8459 StartY=107.278 StartZ=0 EndX=13.8459 EndY=84.0303 EndZ=0
    g3: LineSegment StartX=11.7204 StartY=107.278 StartZ=0 EndX=11.7204 EndY=84.0303 EndZ=0
    g4: ArcOfCircle CenterX=-13.3939 CenterY=108.813 CenterZ=0 NormalX=0 NormalY=0 NormalZ=1 AngleXU=0 Radius=1.06277 StartAngle=1.5708 EndAngle=4.71239
    g5: ArcOfCircle CenterX=6.99051 CenterY=108.813 CenterZ=0 NormalX=0 NormalY=0 NormalZ=1 AngleXU=0 Radius=1.06277 StartAngle=4.71239 EndAngle=7.85398
    g6: LineSegment StartX=-13.3939 StartY=109.876 StartZ=0 EndX=6.99051 EndY=109.876 EndZ=0
    g7: LineSegment StartX=-13.3939 StartY=107.75 StartZ=0 EndX=6.99051 EndY=107.75 EndZ=0
    g8: ArcOfCircle CenterX=-13.496 CenterY=93.656 CenterZ=0 NormalX=0 NormalY=0 NormalZ=1 AngleXU=0 Radius=1.06277 StartAngle=1.5708 EndAngle=4.71239
    g9: ArcOfCircle CenterX=6.96951 CenterY=93.656 CenterZ=0 NormalX=0 NormalY=0 NormalZ=1 AngleXU=0 Radius=1.06277 StartAngle=4.71239 EndAngle=7.85398
    g10: LineSegment StartX=-13.496 StartY=94.7188 StartZ=0 EndX=6.96951 EndY=94.7188 EndZ=0
    g11: LineSegment StartX=-13.496 StartY=92.5933 StartZ=0 EndX=6.96951 EndY=92.5933 EndZ=0
  constraints (20):
    c: Tangent(g0,g2) = 1.5708
    c: Tangent(g0,g3) = -1.5708
    c: Tangent(g1,g2) = 1.5708
    c: Tangent(g1,g3) = -1.5708
    c: Equal(g0,g1)
    c: Vertical(g2)
    c: Tangent(g4,g6) = 1.5708
    c: Tangent(g4,g7) = -1.5708
    c: Tangent(g5,g6) = 1.5708
    c: Tangent(g5,g7) = -1.5708
    c: Equal(g4,g5)
    c: Horizontal(g6)
    c: Tangent(g8,g10) = 1.5708
    c: Tangent(g8,g11) = -1.5708
    c: Tangent(g9,g10) = 1.5708
    c: Tangent(g9,g11) = -1.5708
    c: Equal(g8,g9)
    c: Horizontal(g10)
    c: Equal(g0,g5)
    c: Equal(g0,g9)
FEATURE [PartDesign::Pocket] Pocket009  label="Pocket THT"
  BaseFeature = -> Pocket008
  Direction = (-1,-1e-16,1e-16)
  Length = 8
  Length2 = 5
  Placement = pos=(62.5,0,0) rot=(0.57735,0.57735,0.57735;2.0944rad)
  Profile = -> Sketch031
  ReferenceAxis = -> Sketch031 [N_Axis]
  Refine = true
  Reversed = true
  Suppressed = false
  Type = 0
FEATURE [Sketcher::SketchObject] Sketch032
  ArcFitTolerance = 0
  AttachmentOffset = pos=(0,0,78.5) rot=(0,0,1;0rad)
  FullyConstrained = true
  MakeInternals = false
  MapMode = 5
  Placement = pos=(78.5,0,0) rot=(0.57735,0.57735,0.57735;2.0944rad)
  sketch-geometry (4):
    g0: LineSegment StartX=-17.5 StartY=57.8 StartZ=0 EndX=-17.5 EndY=20.8 EndZ=0
    g1: LineSegment StartX=-17.5 StartY=20.8 StartZ=0 EndX=17.5 EndY=20.8 EndZ=0
    g2: LineSegment StartX=17.5 StartY=20.8 StartZ=0 EndX=17.5 EndY=57.8 EndZ=0
    g3: LineSegment StartX=17.5 StartY=57.8 StartZ=0 EndX=-17.5 EndY=57.8 EndZ=0
  constraints (11):
    c: Coincident(g0,g1)
    c: Coincident(g1,g2)
    c: Coincident(g2,g3)
    c: Coincident(g3,g0)
    c: Vertical(g0)
    c: Vertical(g2)
    c: Horizontal(g1)
    c: DistanceX(g3,g3) = 35
    c: DistanceY(g0,g0) = 37
    c: Symmetric(g0,g2,g-2)
    c: DistanceY(g-1,g0) = 20.8
FEATURE [PartDesign::Pocket] Pocket010  label="Pocket PCB slot"
  BaseFeature = -> Hole006
  Direction = (-1,-1e-16,1e-16)
  Length = 5
  Length2 = 5
  Placement = pos=(0,0,0) rot=(1,0,0;1.5708rad)
  Profile = -> Sketch032
  ReferenceAxis = -> Sketch032 [N_Axis]
  Refine = true
  Suppressed = false
  Type = 1
FEATURE [Sketcher::SketchObject] Sketch033
  ArcFitTolerance = 0
  FullyConstrained = true
  MakeInternals = false
  MapMode = 5
  Placement = pos=(0,0,0) rot=(1,0,0;1.5708rad)
  sketch-geometry (4):
    g0: LineSegment StartX=71.9 StartY=49 StartZ=0 EndX=71.9 EndY=34 EndZ=0
    g1: LineSegment StartX=71.9 StartY=34 StartZ=0 EndX=76.9 EndY=34 EndZ=0
    g2: LineSegment StartX=76.9 StartY=34 StartZ=0 EndX=76.9 EndY=49 EndZ=0
    g3: LineSegment StartX=76.9 StartY=49 StartZ=0 EndX=71.9 EndY=49 EndZ=0
  constraints (12):
    c: Coincident(g0,g1)
    c: Coincident(g1,g2)
    c: Coincident(g2,g3)
    c: Coincident(g3,g0)
    c: Vertical(g0)
    c: Vertical(g2)
    c: Horizontal(g1)
    c: Horizontal(g3)
    c: DistanceX(g-1,g0) = 71.9
    c: DistanceX(g1,g1) = 5
    c: DistanceY(g0,g0) = 15
    c: DistanceY(g-1,g0) = 34
FEATURE [PartDesign::Pocket] Pocket011  label="Pocket Connector"
  BaseFeature = -> Pocket010
  Direction = (0,1,-2e-16)
  Length = 5
  Length2 = 5
  Midplane = true
  Placement = pos=(0,0,0) rot=(1,0,0;1.5708rad)
  Profile = -> Sketch033
  ReferenceAxis = -> Sketch033 [N_Axis]
  Refine = true
  Suppressed = false
  Type = 1
FEATURE [Sketcher::SketchObject] Sketch034
  ArcFitTolerance = 0
  AttachmentOffset = pos=(0,0,80) rot=(0,0,1;0rad)
  FullyConstrained = false
  MakeInternals = false
  MapMode = 5
  Placement = pos=(80,0,0) rot=(0.57735,0.57735,0.57735;2.0944rad)
  sketch-geometry (17):
    g0: ArcOfCircle CenterX=-14.4011 CenterY=46.6696 CenterZ=0 NormalX=0 NormalY=0 NormalZ=1 AngleXU=0 Radius=1 StartAngle=-1.8e-15 EndAngle=3.14159
    g1: ArcOfCircle CenterX=-14.4011 CenterY=36.32 CenterZ=0 NormalX=0 NormalY=0 NormalZ=1 AngleXU=0 Radius=1 StartAngle=3.14159 EndAngle=6.28319
    g2: LineSegment StartX=-13.4011 StartY=46.6696 StartZ=0 EndX=-13.4011 EndY=36.32 EndZ=0
    g3: LineSegment StartX=-15.4011 StartY=46.6696 StartZ=0 EndX=-15.4011 EndY=36.32 EndZ=0
    g4: ArcOfCircle CenterX=14.4011 CenterY=46.6696 CenterZ=0 NormalX=0 NormalY=0 NormalZ=1 AngleXU=0 Radius=1 StartAngle=2.7e-15 EndAngle=3.14159
    g5: ArcOfCircle CenterX=14.4011 CenterY=36.32 CenterZ=0 NormalX=0 NormalY=0 NormalZ=1 AngleXU=0 Radius=1 StartAngle=3.14159 EndAngle=6.28319
    g6: LineSegment StartX=15.4011 StartY=46.6696 StartZ=0 EndX=15.4011 EndY=36.32 EndZ=0
    g7: LineSegment StartX=13.4011 StartY=46.6696 StartZ=0 EndX=13.4011 EndY=36.32 EndZ=0
    g8: LineSegment [constr] StartX=12.75 StartY=25.9438 StartZ=0 EndX=12.75 EndY=52.9438 EndZ=0
    g9: LineSegment [constr] StartX=12.75 StartY=52.9438 StartZ=0 EndX=-12.75 EndY=52.9438 EndZ=0
    g10: LineSegment [constr] StartX=-12.75 StartY=52.9438 StartZ=0 EndX=-12.75 EndY=25.9438 EndZ=0
    g11: LineSegment [constr] StartX=-12.75 StartY=25.9438 StartZ=0 EndX=12.75 EndY=25.9438 EndZ=0
    g12: GeomPoint [constr] X=1e-16 Y=39.4438 Z=0
    g13: Circle CenterX=-12.75 CenterY=52.9438 CenterZ=0 NormalX=0 NormalY=0 NormalZ=1 AngleXU=0 Radius=1.5
    g14: Circle CenterX=12.75 CenterY=52.9438 CenterZ=0 NormalX=0 NormalY=0 NormalZ=1 AngleXU=0 Radius=1.5
    g15: Circle CenterX=12.75 CenterY=25.9438 CenterZ=0 NormalX=0 NormalY=0 NormalZ=1 AngleXU=0 Radius=1.5
    g16: Circle CenterX=-12.75 CenterY=25.9438 CenterZ=0 NormalX=0 NormalY=0 NormalZ=1 AngleXU=0 Radius=1.5
  constraints (34):
    c: Tangent(g0,g2) = 1.5708
    c: Tangent(g0,g3) = -1.5708
    c: Tangent(g1,g2) = 1.5708
    c: Tangent(g1,g3) = -1.5708
    c: Equal(g0,g1)
    c: Vertical(g2)
    c: Tangent(g4,g6) = 1.5708
    c: Tangent(g4,g7) = -1.5708
    c: Tangent(g5,g6) = 1.5708
    c: Tangent(g5,g7) = -1.5708
    c: Equal(g4,g5)
    c: Vertical(g6)
    c: Equal(g0,g4)
    c: Equal(g7,g2)
    c: Symmetric(g0,g4,g-2)
    c: Coincident(g8,g9)
    c: Coincident(g9,g10)
    c: Coincident(g10,g11)
    c: Coincident(g11,g8)
    c: Vertical(g8)
    c: Vertical(g10)
    c: Horizontal(g11)
    c: Symmetric(g10,g8,g12)
    c: Coincident(g13,g9)
    c: Coincident(g14,g8)
    c: Coincident(g15,g8)
    c: Coincident(g16,g10)
    c: Diameter(g13) = 3
    c: DistanceX(g9,g9) = 25.5
    c: DistanceY(g10,g10) = 27
    c: Equal(g13,g16)
    c: Equal(g16,g15)
    c: Equal(g15,g14)
    c: Symmetric(g9,g8,g-2)
FEATURE [PartDesign::Pocket] Pocket012  label="Pocket PCB holes mount+THT"
  BaseFeature = -> Pocket011
  Direction = (-1,-1e-16,1e-16)
  Length = 5
  Length2 = 5
  Placement = pos=(0,0,0) rot=(1,0,0;1.5708rad)
  Profile = -> Sketch034
  ReferenceAxis = -> Sketch034 [N_Axis]
  Refine = true
  Suppressed = false
  Type = 1
FEATURE [Sketcher::SketchObject] Sketch025
  ArcFitTolerance = 0
  FullyConstrained = true
  MakeInternals = false
  MapMode = 5
  Placement = pos=(0,0,0) rot=(0.57735,0.57735,0.57735;2.0944rad)
  expr: Constraints[10] = Sketch022.Constraints.magA
  expr: Constraints[11] = Sketch022.Constraints.magA2
  expr: Constraints[12] = Sketch022.Constraints.magnetoffset
  sketch-geometry (5):
    g0: ArcOfCircle CenterX=-8 CenterY=32.4 CenterZ=0 NormalX=0 NormalY=0 NormalZ=1 AngleXU=0 Radius=2.3 StartAngle=1.5708 EndAngle=4.71239
    g1: ArcOfCircle CenterX=8 CenterY=32.4 CenterZ=0 NormalX=0 NormalY=0 NormalZ=1 AngleXU=0 Radius=2.3 StartAngle=4.71239 EndAngle=7.85398
    g2: LineSegment StartX=-8 StartY=34.7 StartZ=0 EndX=8 EndY=34.7 EndZ=0
    g3: LineSegment StartX=-8 StartY=30.1 StartZ=0 EndX=8 EndY=30.1 EndZ=0
    g4: LineSegment [constr] StartX=-10.3 StartY=32.4 StartZ=0 EndX=10.3 EndY=32.4 EndZ=0
  constraints (13):
    c: Tangent(g0,g2) = 1.5708
    c: Tangent(g0,g3) = -1.5708
    c: Tangent(g1,g2) = 1.5708
    c: Tangent(g1,g3) = -1.5708
    c: Equal(g0,g1)
    c: Symmetric(g1,g0,g-2)
    c: Horizontal(g4)
    c: PointOnObject(g4,g0)
    c: PointOnObject(g4,g1)
    c: PointOnObject(g0,g4)
    c: DistanceX(g4,g4) = 20.6
    c: DistanceY(g0,g0) = 4.6
    c: DistanceY(g-1,g0) = 32.4
FEATURE [Sketcher::SketchObject] Sketch024
  ArcFitTolerance = 0
  AttachmentOffset = pos=(0,0,71.5) rot=(0,0,1;0rad)
  FullyConstrained = true
  MakeInternals = false
  MapMode = 5
  Placement = pos=(71.5,0,0) rot=(0.57735,0.57735,0.57735;2.0944rad)
  expr: .AttachmentOffset.Base.z = 69.5 mm + 2 mm
  expr: .Constraints.magnetoffset = Sketch022.Constraints.magnetoffset
  expr: Constraints[11] = Sketch026.Constraints.magB
  expr: Constraints[5] = Sketch026.Constraints.magB2
  sketch-geometry (5):
    g0: ArcOfCircle CenterX=-10.8 CenterY=32.4 CenterZ=0 NormalX=0 NormalY=0 NormalZ=1 AngleXU=0 Radius=2.35 StartAngle=1.5708 EndAngle=4.71239
    g1: ArcOfCircle CenterX=10.8 CenterY=32.4 CenterZ=0 NormalX=0 NormalY=0 NormalZ=1 AngleXU=0 Radius=2.35 StartAngle=4.71239 EndAngle=7.85398
    g2: LineSegment StartX=-10.8 StartY=34.75 StartZ=0 EndX=10.8 EndY=34.75 EndZ=0
    g3: LineSegment StartX=-10.8 StartY=30.05 StartZ=0 EndX=10.8 EndY=30.05 EndZ=0
    g4: LineSegment [constr] StartX=-13.15 StartY=32.4 StartZ=0 EndX=13.15 EndY=32.4 EndZ=0
  constraints (13):
    c: Tangent(g0,g2) = 1.5708
    c: Tangent(g0,g3) = -1.5708
    c: Tangent(g1,g2) = 1.5708
    c: Tangent(g1,g3) = -1.5708
    c: Equal(g0,g1)
    c: DistanceY(g0,g0) = 4.7
    c: Symmetric(g0,g1,g-2)
    c: Horizontal(g4)
    c: PointOnObject(g4,g0)
    c: PointOnObject(g4,g1)
    c: PointOnObject(g0,g4)
    c: DistanceX(g4,g4) = 26.3
    c: DistanceY(g-1,g4) = 32.4  'magnetoffset'
FEATURE [PartDesign::Body] Body001  label="Wall Mount"
  AllowCompound = false
  Group = -> [Sketch018,Pad001,Sketch019,Pocket,Sketch020,Pocket002,Sketch021,Hole006,Sketch024,Sketch025,Sketch032,Pocket010,Sketch033,Pocket011,Sketch034,Pocket012]
  Origin = -> Origin001
  Tip = -> Pocket012
FEATURE [Sketcher::SketchObject] Sketch035
  ArcFitTolerance = 0
  FullyConstrained = true
  MakeInternals = false
  MapMode = 5
  Placement = pos=(0,0,0) rot=(1,0,0;1.5708rad)
  sketch-geometry (30):
    g0: LineSegment StartX=5.8 StartY=31.2 StartZ=0 EndX=6.7805 EndY=0 EndZ=0
    g1: LineSegment StartX=6.7805 StartY=0 StartZ=0 EndX=13.2 EndY=0 EndZ=0
    g2: LineSegment StartX=13.2 StartY=0 StartZ=0 EndX=13.2 EndY=2 EndZ=0
    g3: LineSegment StartX=13.2 StartY=2 StartZ=0 EndX=8.71765 EndY=2 EndZ=0
    g4: LineSegment StartX=8.71765 StartY=2 StartZ=0 EndX=8.57937 EndY=6.4 EndZ=0
    g5: LineSegment StartX=8.57937 StartY=6.4 StartZ=0 EndX=12.4 EndY=6.4 EndZ=0
    g6: LineSegment StartX=12.4 StartY=6.4 StartZ=0 EndX=12.4 EndY=8.4 EndZ=0
    g7: LineSegment StartX=12.4 StartY=8.4 StartZ=0 EndX=8.51652 EndY=8.4 EndZ=0
    g8: LineSegment StartX=8.51652 StartY=8.4 StartZ=0 EndX=8.45367 EndY=10.4 EndZ=0
    g9: LineSegment StartX=8.45367 StartY=10.4 StartZ=0 EndX=11.25 EndY=10.4 EndZ=0
    g10: LineSegment StartX=11.25 StartY=10.4 StartZ=0 EndX=11.25 EndY=12.4 EndZ=0
    g11: LineSegment StartX=11.25 StartY=12.4 StartZ=0 EndX=8.39081 EndY=12.4 EndZ=0
    g12: LineSegment StartX=8.39081 StartY=12.4 StartZ=0 EndX=8.32796 EndY=14.4 EndZ=0
    g13: LineSegment StartX=8.32796 StartY=14.4 StartZ=0 EndX=10.5 EndY=14.4 EndZ=0
    g14: LineSegment StartX=10.5 StartY=14.4 StartZ=0 EndX=10.5 EndY=16.4 EndZ=0
    g15: LineSegment StartX=10.5 StartY=16.4 StartZ=0 EndX=8.26511 EndY=16.4 EndZ=0
    g16: LineSegment StartX=8.26511 StartY=16.4 StartZ=0 EndX=8.17712 EndY=19.2 EndZ=0
    g17: LineSegment StartX=8.17712 StartY=19.2 StartZ=0 EndX=10.1 EndY=19.2 EndZ=0
    g18: LineSegment StartX=10.1 StartY=19.2 StartZ=0 EndX=10.1 EndY=20.4 EndZ=0
    g19: LineSegment StartX=10.1 StartY=20.4 StartZ=0 EndX=8.1394 EndY=20.4 EndZ=0
    g20: LineSegment StartX=8.1394 StartY=20.4 StartZ=0 EndX=8.05141 EndY=23.2 EndZ=0
    g21: LineSegment StartX=8.05141 StartY=23.2 StartZ=0 EndX=10.1 EndY=23.2 EndZ=0
    g22: LineSegment StartX=10.1 StartY=23.2 StartZ=0 EndX=10.1 EndY=24.4 EndZ=0
    g23: LineSegment StartX=10.1 StartY=24.4 StartZ=0 EndX=8.0137 EndY=24.4 EndZ=0
    g24: LineSegment StartX=8.0137 StartY=24.4 StartZ=0 EndX=7.92571 EndY=27.2 EndZ=0
    g25: LineSegment StartX=7.92571 StartY=27.2 StartZ=0 EndX=10.1 EndY=27.2 EndZ=0
    g26: LineSegment StartX=10.1 StartY=27.2 StartZ=0 EndX=10.1 EndY=28.4 EndZ=0
    g27: LineSegment StartX=10.1 StartY=28.4 StartZ=0 EndX=7.88799 EndY=28.4 EndZ=0
    g28: LineSegment StartX=7.88799 StartY=28.4 StartZ=0 EndX=7.8 EndY=31.2 EndZ=0
    g29: LineSegment StartX=7.8 StartY=31.2 StartZ=0 EndX=5.8 EndY=31.2 EndZ=0
  constraints (90):
    c: Coincident(g0,g1)
    c: Horizontal(g1)
    c: Coincident(g1,g2)
    c: Coincident(g2,g3)
    c: Horizontal(g3)
    c: Coincident(g3,g4)
    c: Coincident(g4,g5)
    c: Horizontal(g5)
    c: Coincident(g5,g6)
    c: Coincident(g6,g7)
    c: Horizontal(g7)
    c: Coincident(g7,g8)
    c: Coincident(g8,g9)
    c: Horizontal(g9)
    c: Coincident(g9,g10)
    c: Vertical(g10)
    c: Coincident(g10,g11)
    c: Horizontal(g11)
    c: Coincident(g11,g12)
    c: Coincident(g12,g13)
    c: Horizontal(g13)
    c: Coincident(g13,g14)
    c: Coincident(g14,g15)
    c: Horizontal(g15)
    c: Coincident(g15,g16)
    c: Coincident(g16,g17)
    c: Coincident(g17,g18)
    c: Coincident(g18,g19)
    c: Horizontal(g19)
    c: Coincident(g19,g20)
    c: Coincident(g20,g21)
    c: Horizontal(g21)
    c: Coincident(g21,g22)
    c: Coincident(g22,g23)
    c: Horizontal(g23)
    c: Coincident(g23,g24)
    c: Coincident(g24,g25)
    c: Horizontal(g25)
    c: Coincident(g25,g26)
    c: Vertical(g26)
    c: Coincident(g26,g27)
    c: Horizontal(g27)
    c: Coincident(g27,g28)
    c: Coincident(g28,g29)
    c: Coincident(g29,g0)
    c: Horizontal(g29)
    c: Angle(g-2,g0) = 0.0314159
    c: DistanceY(g0,g0) = 31.2
    c: DistanceX(g-1,g1) = 13.2
    c: Vertical(g2)
    c: Vertical(g14)
    c: Horizontal(g17)
    c: Vertical(g22)
    c: Vertical(g18)
    c: Vertical(g6)
    c: DistanceY(g2,g2) = 2
    c: Equal(g2,g6)
    c: Equal(g6,g10)
    c: Equal(g10,g14)
    c: DistanceY(g4,g4) = 4.4
    c: Equal(g8,g12)
    c: DistanceY(g8,g8) = 2
    c: DistanceY(g18,g18) = 1.2
    c: Equal(g26,g22)
    c: Equal(g22,g18)
    c: Equal(g16,g20)
    c: Equal(g20,g24)
    c: DistanceY(g16,g16) = 2.8
    c: Parallel(g0,g28)
    c: Parallel(g0,g24)
    c: Parallel(g20,g0)
    c: Parallel(g0,g16)
    c: Parallel(g0,g12)
    c: Parallel(g0,g8)
    c: Parallel(g0,g4)
    c: PointOnObject(g7,g4)
    c: PointOnObject(g11,g8)
    c: PointOnObject(g15,g12)
    c: PointOnObject(g19,g16)
    c: PointOnObject(g23,g20)
    c: PointOnObject(g27,g24)
    c: DistanceX(g29,g29) = 2
    c: DistanceX(g-1,g5) = 12.4
    c: DistanceX(g-1,g9) = 11.25
    c: DistanceX(g-1,g13) = 10.5
    c: DistanceX(g-1,g17) = 10.1
    c: PointOnObject(g21,g18)
    c: PointOnObject(g25,g22)
    c: PointOnObject(g-1,g1)
    c: DistanceX(g-1,g0) = 5.8
FEATURE [PartDesign::Revolution] Revolution001
  Angle = 360
  Angle2 = 60
  Axis = (0,2e-16,1)
  Base = (0,0,0)
  Placement = pos=(0,0,0) rot=(1,0,0;1.5708rad)
  Profile = -> Sketch035
  ReferenceAxis = -> Sketch035 [V_Axis]
  Refine = true
  Reversed = true
  Suppressed = false
  Type = 0
FEATURE [PartDesign::Body] Body003  label="Liquor pourer stopper"
  AllowCompound = false
  Group = -> [Sketch035,Revolution001]
  Origin = -> Origin003
  Placement = pos=(0,0,30.1095) rot=(0,0,1;0rad)
  Tip = -> Revolution001
FEATURE [Mesh::Feature] OBJ_PCB  label="PCB SLOT V2.2"
  Placement = pos=(74.93,-0.02,39.35) rot=(0.57735,-0.57735,-0.57735;2.0944rad)
FEATURE [Mesh::Feature] OBJ_PCB001  label="PCB Dispenser V2.003"
  Placement = pos=(61.8,0,74) rot=(0.57735,-0.57735,-0.57735;2.0944rad)
FEATURE [Sketcher::SketchObject] Sketch036
  ArcFitTolerance = 1e-06
  AttachmentOffset = pos=(0,0,71.9) rot=(0,0,1;0rad)
  AttachmentSupport = -> [YZ_Plane002]
  FullyConstrained = false
  MakeInternals = false
  MapMode = 5
  Placement = pos=(71.9,0,0) rot=(0.57735,0.57735,0.57735;2.0944rad)
  expr: .AttachmentOffset.Base.z = Sketch018.Constraints.width
  expr: Constraints[29] = Sketch027.Placement.Base.z - Pad003.Length
  expr: Constraints[30] = Sketch030.Constraints.PCBhieght
  expr: Constraints[31] = Sketch022.Constraints.Width
  sketch-geometry (14):
    g0: LineSegment [constr] StartX=-5 StartY=144.1 StartZ=0 EndX=5 EndY=144.1 EndZ=0
    g1: LineSegment [constr] StartX=5 StartY=144.1 StartZ=0 EndX=5 EndY=159.1 EndZ=0
    g2: LineSegment [constr] StartX=5 StartY=159.1 StartZ=0 EndX=-5 EndY=159.1 EndZ=0
    g3: LineSegment [constr] StartX=-5 StartY=159.1 StartZ=0 EndX=-5 EndY=144.1 EndZ=0
    g4: GeomPoint [constr] X=0 Y=151.6 Z=0
    g5: Circle CenterX=-5 CenterY=159.1 CenterZ=0 NormalX=0 NormalY=0 NormalZ=1 AngleXU=0 Radius=2.63845
    g6: Circle CenterX=5 CenterY=159.1 CenterZ=0 NormalX=0 NormalY=0 NormalZ=1 AngleXU=0 Radius=2.63845
    g7: Circle CenterX=5 CenterY=144.1 CenterZ=0 NormalX=0 NormalY=0 NormalZ=1 AngleXU=0 Radius=2.63845
    g8: Circle CenterX=-5 CenterY=144.1 CenterZ=0 NormalX=0 NormalY=0 NormalZ=1 AngleXU=0 Radius=2.63845
    g9: LineSegment StartX=-17.5 StartY=118.2 StartZ=0 EndX=17.5 EndY=118.2 EndZ=0
    g10: LineSegment StartX=17.5 StartY=118.2 StartZ=0 EndX=17.5 EndY=185 EndZ=0
    g11: LineSegment StartX=17.5 StartY=185 StartZ=0 EndX=-17.5 EndY=185 EndZ=0
    g12: LineSegment StartX=-17.5 StartY=185 StartZ=0 EndX=-17.5 EndY=118.2 EndZ=0
    g13: GeomPoint [constr] X=0 Y=151.6 Z=0
  constraints (32):
    c: Coincident(g0,g1)
    c: Coincident(g1,g2)
    c: Coincident(g2,g3)
    c: Coincident(g3,g0)
    c: Horizontal(g0)
    c: Horizontal(g2)
    c: Vertical(g1)
    c: Vertical(g3)
    c: Symmetric(g2,g0,g4)
    c: PointOnObject(g4,g-2)
    c: Coincident(g5,g2)
    c: Coincident(g6,g1)
    c: Coincident(g7,g0)
    c: Coincident(g8,g0)
    c: Equal(g5,g6)
    c: Equal(g6,g7)
    c: Equal(g7,g8)
    c: DistanceX(g2,g2) = 10
    c: DistanceY(g3,g3) = 15
    c: Coincident(g9,g10)
    c: Coincident(g10,g11)
    c: Coincident(g11,g12)
    c: Coincident(g12,g9)
    c: Horizontal(g9)
    c: Horizontal(g11)
    c: Vertical(g10)
    c: Vertical(g12)
    c: Symmetric(g11,g9,g13)
    c: Coincident(g13,g4)
    c: DistanceY(g-1,g10) = 185
    c: DistanceY(g-1,g9) = 118.2
    c: DistanceX(g11,g11) = 35
FEATURE [PartDesign::Hole] Hole008  label="Hole Mouning Air Valve"
  BaseFeature = -> Pocket009
  CustomThreadClearance = 0
  Depth = 468.454
  DepthType = 1
  Diameter = 3
  DrillForDepth = false
  DrillPoint = 1
  DrillPointAngle = 118
  HoleCutCountersinkAngle = 90
  HoleCutCustomValues = false
  HoleCutDepth = 7.3
  HoleCutDiameter = 5.7
  HoleCutType = 1
  ModelThread = false
  Placement = pos=(62.5,0,0) rot=(0.57735,0.57735,0.57735;2.0944rad)
  Profile = -> Sketch036
  Refine = true
  Suppressed = false
  Tapered = false
  TaperedAngle = 90
  ThreadClass = 0
  ThreadDepth = 468.454
  ThreadDepthType = 0
  ThreadDirection = 0
  ThreadFit = 0
  ThreadSize = 0
  ThreadType = 0
  Threaded = false
  UseCustomThreadClearance = false
  expr: HoleCutDepth = 9.3 - 2
  expr: HoleCutDiameter = 5.4 + 0.3
FEATURE [Sketcher::SketchObject] Sketch037
  ArcFitTolerance = 1e-06
  AttachmentOffset = pos=(0,0,65.5) rot=(0,0,1;0rad)
  AttachmentSupport = -> [YZ_Plane002]
  FullyConstrained = false
  MakeInternals = false
  MapMode = 5
  Placement = pos=(65.5,0,0) rot=(0.57735,0.57735,0.57735;2.0944rad)
  expr: .AttachmentOffset.Base.z = 62.5 mm + 3 mm
  sketch-geometry (4):
    g0: LineSegment StartX=-11.7153 StartY=166.198 StartZ=0 EndX=-11.7153 EndY=130.747 EndZ=0
    g1: LineSegment StartX=-11.7153 StartY=130.747 StartZ=0 EndX=12.7893 EndY=130.747 EndZ=0
    g2: LineSegment StartX=12.7893 StartY=130.747 StartZ=0 EndX=12.7893 EndY=166.198 EndZ=0
    g3: LineSegment StartX=12.7893 StartY=166.198 StartZ=0 EndX=-11.7153 EndY=166.198 EndZ=0
  constraints (8):
    c: Coincident(g0,g1)
    c: Coincident(g1,g2)
    c: Coincident(g2,g3)
    c: Coincident(g3,g0)
    c: Vertical(g0)
    c: Vertical(g2)
    c: Horizontal(g1)
    c: Horizontal(g3)
FEATURE [PartDesign::Pad] Pad004  label="Pad Better printable 1"
  BaseFeature = -> Hole008
  Direction = (1,0,0)
  Length = 0.2
  Length2 = 10
  Placement = pos=(62.5,0,0) rot=(0.57735,0.57735,0.57735;2.0944rad)
  Profile = -> Sketch037
  ReferenceAxis = -> Sketch037 [N_Axis]
  Refine = true
  Reversed = true
  Suppressed = false
  Type = 0
FEATURE [Sketcher::SketchObject] Sketch038
  ArcFitTolerance = 1e-06
  AttachmentOffset = pos=(0,0,67.7) rot=(0,0,1;0rad)
  AttachmentSupport = -> [YZ_Plane002]
  FullyConstrained = false
  MakeInternals = false
  MapMode = 5
  Placement = pos=(67.7,0,0) rot=(0.57735,0.57735,0.57735;2.0944rad)
  expr: .AttachmentOffset.Base.z = Sketch018.Constraints.width - 4.2 mm
  sketch-geometry (2):
    g0: Circle CenterX=-12.5803 CenterY=9.90761 CenterZ=0 NormalX=0 NormalY=0 NormalZ=1 AngleXU=0 Radius=4.61491
    g1: Circle CenterX=12.4213 CenterY=10.0752 CenterZ=0 NormalX=0 NormalY=0 NormalZ=1 AngleXU=0 Radius=4.03557
FEATURE [PartDesign::Pad] Pad005  label="Pad Better printable 2"
  BaseFeature = -> Pad004
  Direction = (1,0,0)
  Length = 0.2
  Length2 = 10
  Placement = pos=(62.5,0,0) rot=(0.57735,0.57735,0.57735;2.0944rad)
  Profile = -> Sketch038
  ReferenceAxis = -> Sketch038 [N_Axis]
  Refine = true
  Reversed = true
  Suppressed = false
  Type = 0
FEATURE [PartDesign::Body] Body002  label="Bottle Holder"
  AllowCompound = false
  Group = -> [Sketch022,Pad002,Sketch023,Hole007,Sketch026,Pocket005,Sketch027,Pad003,Sketch028,Pocket006,Sketch030,Pocket008,Sketch031,Pocket009,Sketch036,Hole008,Sketch037,Pad004,Sketch038,Pad005]
  Origin = -> Origin002
  Tip = -> Pad005
FEATURE [Part::FeaturePython] b_Air_Valve_WCD130_24B_001_  label="Air Valve WCD130-24B_001"  # a2plus imported part (geometry in sourceFile) (typed FeaturePython)
  Placement = pos=(52.5209,-0.3663,136.231) rot=(0.57735,-0.57735,-0.57735;2.0944rad)
  a2p_Version = 0.4.68
  fixedPosition = true
  objectType = a2pPart
  sourceFile = ./../PreMade/Air Valve WCD130-24B.FCStd
  subassemblyImport = false
  timeLastImport = 1.74473e+09
  updateColors = true
